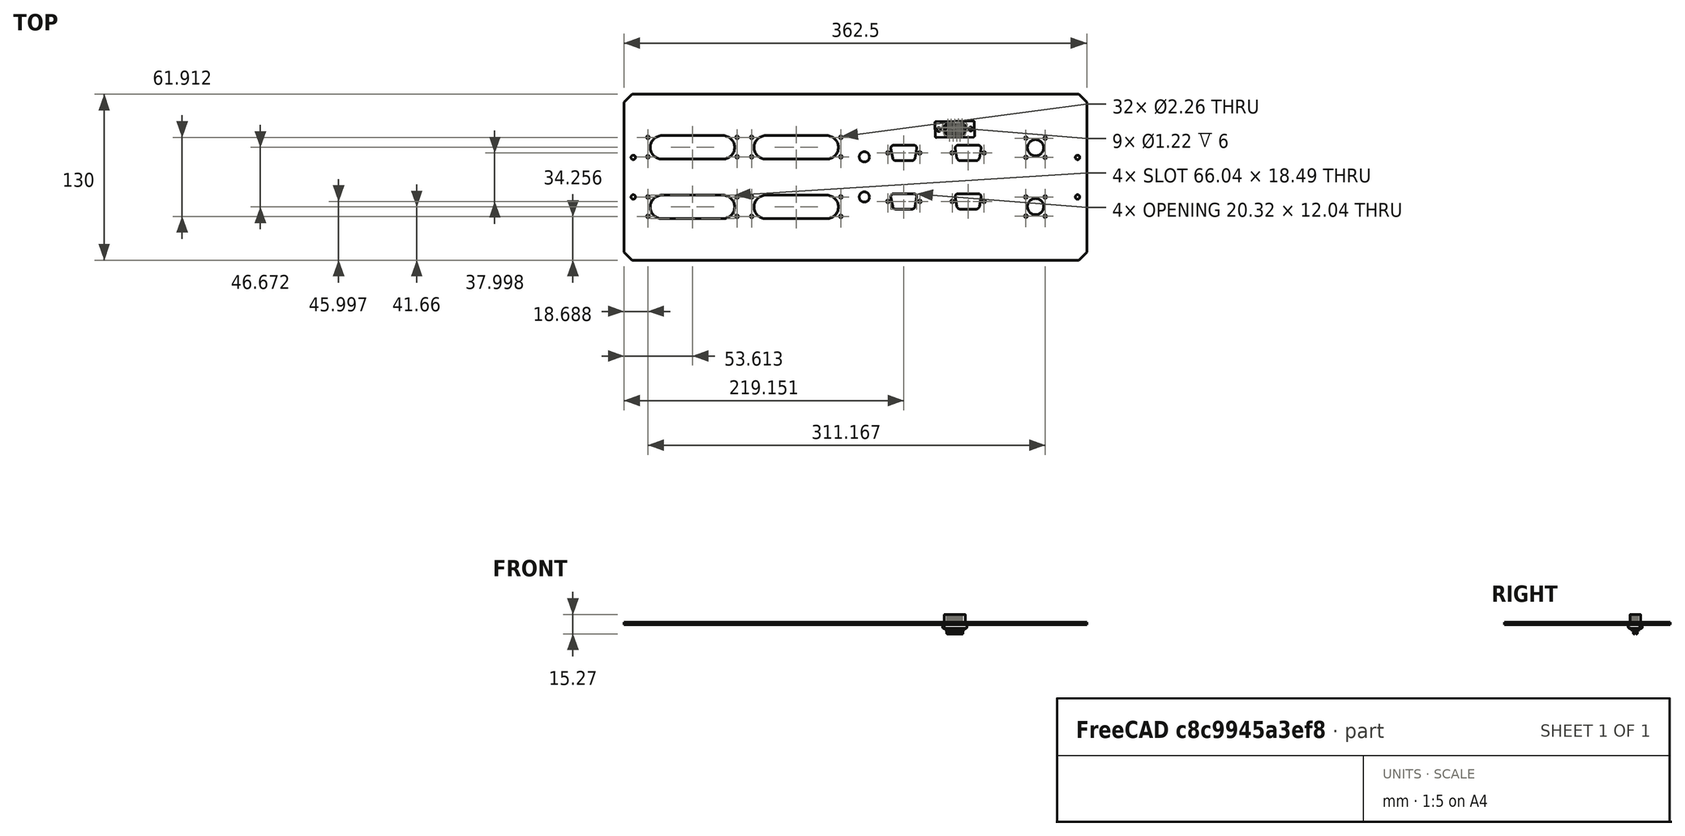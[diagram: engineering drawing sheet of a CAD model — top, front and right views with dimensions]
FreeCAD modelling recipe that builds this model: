
FCSTD DOCUMENT  (FreeCAD 0.20R29603 (Git))
Label: DCT_Front_Panel
License: All rights reserved
LicenseURL: http://en.wikipedia.org/wiki/All_rights_reserved
objects: TechDraw::DrawViewDimension×33, Sketcher::SketchObject×10, TechDraw::DrawViewPart×5, PartDesign::Pocket×4, PartDesign::Line×2, PartDesign::ShapeBinder×2, Part::Refine×1, Part::Feature×1, PartDesign::FeatureBase×1, TechDraw::DrawSVGTemplate×1, TechDraw::DrawViewAnnotation×1, PartDesign::Body×1, TechDraw::DrawPage×1
note: 26 computed .brp shape members not serialized (recipe doc carries the construction recipe); baked Part::Feature solids carry a one-line shape summary decoded from their .brp

FEATURE [Part::Refine] Part__Feature041002002  label="171-009-206"
  Placement = pos=(159.218,43.3941,68.1309) rot=(0,0,1;0.015493rad)
FEATURE [Part::Feature] BaseFeature001  label="Panel001"
  Placement = pos=(44.8215,92.0039,-3.8) rot=(0,0,1;0rad)
  shape: bbox 362.5 x 130 x 2 mm, 14 faces (baked)
FEATURE [PartDesign::FeatureBase] BaseFeature
  BaseFeature = -> BaseFeature001
FEATURE [PartDesign::Line] DatumLine
  AttacherType = Attacher::AttachEngineLine
  Length = 20
  MapMode = 43
  Placement = pos=(51.8643,0,71.9309) rot=(0,0.707107,0.707107;3.14159rad)
  ResizeMode = 0
  Support = -> [BaseFeature]
FEATURE [Sketcher::SketchObject] Sketch002  label="All_Feed_Throughs"
  ExternalGeometry = -> [BaseFeature,DatumLine]
  FullyConstrained = true
  MapMode = 5
  Placement = pos=(0,0,71.9309) rot=(0,0,1;0rad)
  Support = -> [BaseFeature]
  expr: Constraints[103] = Constraints[21]
  expr: Constraints[104] = Constraints[22]
  sketch-geometry (121):
    g0: ArcOfCircle CenterX=-18.2685 CenterY=-53.6783 CenterZ=0 NormalX=0 NormalY=0 NormalZ=1 AngleXU=0 Radius=9.2456 StartAngle=1.5708 EndAngle=4.71239
    g1: ArcOfCircle CenterX=29.2803 CenterY=-53.6783 CenterZ=0 NormalX=0 NormalY=0 NormalZ=1 AngleXU=0 Radius=9.2456 StartAngle=4.71239 EndAngle=7.85398
    g2: LineSegment StartX=-18.2685 StartY=-62.9239 StartZ=0 EndX=29.2803 EndY=-62.9239 EndZ=0
    g3: LineSegment StartX=29.2803 StartY=-44.4327 StartZ=0 EndX=-18.2685 EndY=-44.4327 EndZ=0
    g4: LineSegment StartX=38.5259 StartY=-63.7494 StartZ=0 EndX=38.5259 EndY=-43.6072 EndZ=0
    g5: LineSegment StartX=-27.5141 StartY=-43.6072 StartZ=0 EndX=-27.5141 EndY=-63.7494 EndZ=0
    g6: LineSegment StartX=-32.0861 StartY=-43.6072 StartZ=0 EndX=43.0979 EndY=-43.6072 EndZ=0
    g7: LineSegment StartX=43.0979 StartY=-43.6072 StartZ=0 EndX=43.0979 EndY=-63.7494 EndZ=0
    g8: LineSegment StartX=43.0979 StartY=-63.7494 StartZ=0 EndX=-32.0861 EndY=-63.7494 EndZ=0
    g9: LineSegment StartX=-32.0861 StartY=-63.7494 StartZ=0 EndX=-32.0861 EndY=-43.6072 EndZ=0
    g10: LineSegment StartX=-27.5141 StartY=-53.6783 StartZ=0 EndX=-32.0861 EndY=-53.6783 EndZ=0
    g11: LineSegment StartX=38.5259 StartY=-53.6783 StartZ=0 EndX=43.0979 EndY=-53.6783 EndZ=0
    g12: LineSegment StartX=5.50594 StartY=-44.4327 StartZ=0 EndX=5.50594 EndY=-43.6072 EndZ=0
    g13: LineSegment StartX=5.50594 StartY=-63.7494 StartZ=0 EndX=5.50594 EndY=-62.9239 EndZ=0
    g14: LineSegment StartX=-27.5141 StartY=-53.6783 StartZ=0 EndX=38.5259 EndY=-53.6783 EndZ=0
    g15: LineSegment StartX=5.50594 StartY=-44.4327 StartZ=0 EndX=5.50594 EndY=-62.9239 EndZ=0
    g16: GeomPoint X=5.50594 Y=-53.6783 Z=0
    g17: LineSegment StartX=38.5259 StartY=-43.6072 StartZ=0 EndX=5.50594 EndY=-43.6072 EndZ=0
    g18: LineSegment StartX=5.50594 StartY=-43.6072 StartZ=0 EndX=-27.5141 EndY=-43.6072 EndZ=0
    g19: LineSegment StartX=-27.5141 StartY=-63.7494 StartZ=0 EndX=-32.0861 EndY=-63.7494 EndZ=0
    g20: LineSegment StartX=43.0979 StartY=-63.7494 StartZ=0 EndX=38.5259 EndY=-63.7494 EndZ=0
    g21: Circle CenterX=40.4309 CenterY=-45.8424 CenterZ=0 NormalX=0 NormalY=0 NormalZ=1 AngleXU=0 Radius=1.1303
    g22: Circle CenterX=40.4309 CenterY=-61.0824 CenterZ=0 NormalX=0 NormalY=0 NormalZ=1 AngleXU=0 Radius=1.1303
    g23: Circle CenterX=-29.4191 CenterY=-45.8424 CenterZ=0 NormalX=0 NormalY=0 NormalZ=1 AngleXU=0 Radius=1.1303
    g24: Circle CenterX=-29.4191 CenterY=-61.0824 CenterZ=0 NormalX=0 NormalY=0 NormalZ=1 AngleXU=0 Radius=1.1303
    g25: LineSegment StartX=40.4309 StartY=-61.0824 StartZ=0 EndX=43.0979 EndY=-61.0824 EndZ=0
    g26: LineSegment StartX=40.4309 StartY=-61.0824 StartZ=0 EndX=40.4309 EndY=-63.7494 EndZ=0
    g27: LineSegment StartX=-29.4191 StartY=-61.0824 StartZ=0 EndX=-29.4191 EndY=-63.7494 EndZ=0
    g28: LineSegment StartX=-29.4191 StartY=-61.0824 StartZ=0 EndX=-32.0861 EndY=-61.0824 EndZ=0
    g29: ArcOfCircle CenterX=-99.5518 CenterY=-53.6783 CenterZ=0 NormalX=0 NormalY=0 NormalZ=1 AngleXU=0 Radius=9.2456 StartAngle=1.5708 EndAngle=4.71239
    g30: ArcOfCircle CenterX=-52.003 CenterY=-53.6783 CenterZ=0 NormalX=0 NormalY=0 NormalZ=1 AngleXU=0 Radius=9.2456 StartAngle=4.71239 EndAngle=7.85398
    g31: LineSegment StartX=-99.5518 StartY=-62.9239 StartZ=0 EndX=-52.003 EndY=-62.9239 EndZ=0
    g32: LineSegment StartX=-52.003 StartY=-44.4327 StartZ=0 EndX=-99.5518 EndY=-44.4327 EndZ=0
    g33: LineSegment StartX=-42.7574 StartY=-63.7494 StartZ=0 EndX=-42.7574 EndY=-43.6072 EndZ=0
    g34: LineSegment StartX=-108.797 StartY=-43.6072 StartZ=0 EndX=-108.797 EndY=-63.7494 EndZ=0
    g35: LineSegment StartX=-113.369 StartY=-43.6072 StartZ=0 EndX=-38.1854 EndY=-43.6072 EndZ=0
    g36: LineSegment StartX=-38.1854 StartY=-43.6072 StartZ=0 EndX=-38.1854 EndY=-63.7494 EndZ=0
    g37: LineSegment StartX=-38.1854 StartY=-63.7494 StartZ=0 EndX=-113.369 EndY=-63.7494 EndZ=0
    g38: LineSegment StartX=-113.369 StartY=-63.7494 StartZ=0 EndX=-113.369 EndY=-43.6072 EndZ=0
    g39: LineSegment StartX=-108.797 StartY=-53.6783 StartZ=0 EndX=-113.369 EndY=-53.6783 EndZ=0
    g40: LineSegment StartX=-42.7574 StartY=-53.6783 StartZ=0 EndX=-38.1854 EndY=-53.6783 EndZ=0
    g41: LineSegment StartX=-75.7774 StartY=-44.4327 StartZ=0 EndX=-75.7774 EndY=-43.6072 EndZ=0
    g42: LineSegment StartX=-75.7774 StartY=-63.7494 StartZ=0 EndX=-75.7774 EndY=-62.9239 EndZ=0
    g43: LineSegment StartX=-108.797 StartY=-53.6783 StartZ=0 EndX=-42.7574 EndY=-53.6783 EndZ=0
    g44: LineSegment StartX=-75.7774 StartY=-44.4327 StartZ=0 EndX=-75.7774 EndY=-62.9239 EndZ=0
    g45: GeomPoint X=-75.7774 Y=-53.6783 Z=0
    g46: LineSegment StartX=-42.7574 StartY=-43.6072 StartZ=0 EndX=-75.7774 EndY=-43.6072 EndZ=0
    g47: LineSegment StartX=-75.7774 StartY=-43.6072 StartZ=0 EndX=-108.797 EndY=-43.6072 EndZ=0
    g48: LineSegment StartX=-108.797 StartY=-63.7494 StartZ=0 EndX=-113.369 EndY=-63.7494 EndZ=0
    g49: LineSegment StartX=-38.1854 StartY=-63.7494 StartZ=0 EndX=-42.7574 EndY=-63.7494 EndZ=0
    g50: Circle CenterX=-40.8524 CenterY=-45.8424 CenterZ=0 NormalX=0 NormalY=0 NormalZ=1 AngleXU=0 Radius=1.1303
    g51: Circle CenterX=-40.8524 CenterY=-61.0824 CenterZ=0 NormalX=0 NormalY=0 NormalZ=1 AngleXU=0 Radius=1.1303
    g52: Circle CenterX=-110.702 CenterY=-45.8424 CenterZ=0 NormalX=0 NormalY=0 NormalZ=1 AngleXU=0 Radius=1.1303
    g53: Circle CenterX=-110.702 CenterY=-61.0824 CenterZ=0 NormalX=0 NormalY=0 NormalZ=1 AngleXU=0 Radius=1.1303
    g54: LineSegment StartX=-40.8524 StartY=-61.0824 StartZ=0 EndX=-38.1854 EndY=-61.0824 EndZ=0
    g55: LineSegment StartX=-40.8524 StartY=-61.0824 StartZ=0 EndX=-40.8524 EndY=-63.7494 EndZ=0
    g56: LineSegment StartX=-110.702 StartY=-61.0824 StartZ=0 EndX=-110.702 EndY=-63.7494 EndZ=0
    g57: LineSegment StartX=-110.702 StartY=-61.0824 StartZ=0 EndX=-113.369 EndY=-61.0824 EndZ=0
    g58: ArcOfCircle CenterX=-18.2685 CenterY=-100.35 CenterZ=0 NormalX=0 NormalY=0 NormalZ=1 AngleXU=0 Radius=9.2456 StartAngle=1.5708 EndAngle=4.71239
    g59: ArcOfCircle CenterX=29.2803 CenterY=-100.35 CenterZ=0 NormalX=0 NormalY=0 NormalZ=1 AngleXU=0 Radius=9.2456 StartAngle=4.71239 EndAngle=7.85398
    g60: LineSegment StartX=-18.2685 StartY=-109.596 StartZ=0 EndX=29.2803 EndY=-109.596 EndZ=0
    g61: LineSegment StartX=29.2803 StartY=-91.1045 StartZ=0 EndX=-18.2685 EndY=-91.1045 EndZ=0
    g62: LineSegment StartX=38.5259 StartY=-110.421 StartZ=0 EndX=38.5259 EndY=-90.279 EndZ=0
    g63: LineSegment StartX=-27.5141 StartY=-90.279 StartZ=0 EndX=-27.5141 EndY=-110.421 EndZ=0
    g64: LineSegment StartX=-32.0861 StartY=-90.279 StartZ=0 EndX=43.0979 EndY=-90.279 EndZ=0
    g65: LineSegment StartX=43.0979 StartY=-90.279 StartZ=0 EndX=43.0979 EndY=-110.421 EndZ=0
    g66: LineSegment StartX=43.0979 StartY=-110.421 StartZ=0 EndX=-32.0861 EndY=-110.421 EndZ=0
    g67: LineSegment StartX=-32.0861 StartY=-110.421 StartZ=0 EndX=-32.0861 EndY=-90.279 EndZ=0
    g68: LineSegment StartX=-27.5141 StartY=-100.35 StartZ=0 EndX=-32.0861 EndY=-100.35 EndZ=0
    g69: LineSegment StartX=38.5259 StartY=-100.35 StartZ=0 EndX=43.0979 EndY=-100.35 EndZ=0
    g70: LineSegment StartX=5.50594 StartY=-91.1045 StartZ=0 EndX=5.50594 EndY=-90.279 EndZ=0
    g71: LineSegment StartX=5.50594 StartY=-110.421 StartZ=0 EndX=5.50594 EndY=-109.596 EndZ=0
    g72: LineSegment StartX=-27.5141 StartY=-100.35 StartZ=0 EndX=38.5259 EndY=-100.35 EndZ=0
    g73: LineSegment StartX=5.50594 StartY=-91.1045 StartZ=0 EndX=5.50594 EndY=-109.596 EndZ=0
    g74: GeomPoint X=5.50594 Y=-100.35 Z=0
    g75: LineSegment StartX=38.5259 StartY=-90.279 StartZ=0 EndX=5.50594 EndY=-90.279 EndZ=0
    g76: LineSegment StartX=5.50594 StartY=-90.279 StartZ=0 EndX=-27.5141 EndY=-90.279 EndZ=0
    g77: LineSegment StartX=-27.5141 StartY=-110.421 StartZ=0 EndX=-32.0861 EndY=-110.421 EndZ=0
    g78: LineSegment StartX=43.0979 StartY=-110.421 StartZ=0 EndX=38.5259 EndY=-110.421 EndZ=0
    g79: Circle CenterX=40.4309 CenterY=-92.5142 CenterZ=0 NormalX=0 NormalY=0 NormalZ=1 AngleXU=0 Radius=1.1303
    g80: Circle CenterX=40.4309 CenterY=-107.754 CenterZ=0 NormalX=0 NormalY=0 NormalZ=1 AngleXU=0 Radius=1.1303
    g81: Circle CenterX=-29.4191 CenterY=-92.5142 CenterZ=0 NormalX=0 NormalY=0 NormalZ=1 AngleXU=0 Radius=1.1303
    g82: Circle CenterX=-29.4191 CenterY=-107.754 CenterZ=0 NormalX=0 NormalY=0 NormalZ=1 AngleXU=0 Radius=1.1303
    g83: LineSegment StartX=40.4309 StartY=-107.754 StartZ=0 EndX=43.0979 EndY=-107.754 EndZ=0
    g84: LineSegment StartX=40.4309 StartY=-107.754 StartZ=0 EndX=40.4309 EndY=-110.421 EndZ=0
    g85: LineSegment StartX=-29.4191 StartY=-107.754 StartZ=0 EndX=-29.4191 EndY=-110.421 EndZ=0
    g86: LineSegment StartX=-29.4191 StartY=-107.754 StartZ=0 EndX=-32.0861 EndY=-107.754 EndZ=0
    g87: ArcOfCircle CenterX=-99.5518 CenterY=-100.35 CenterZ=0 NormalX=0 NormalY=0 NormalZ=1 AngleXU=0 Radius=9.2456 StartAngle=1.5708 EndAngle=4.71239
    g88: ArcOfCircle CenterX=-52.003 CenterY=-100.35 CenterZ=0 NormalX=0 NormalY=0 NormalZ=1 AngleXU=0 Radius=9.2456 StartAngle=4.71239 EndAngle=7.85398
    g89: LineSegment StartX=-99.5518 StartY=-109.596 StartZ=0 EndX=-52.003 EndY=-109.596 EndZ=0
    g90: LineSegment StartX=-52.003 StartY=-91.1045 StartZ=0 EndX=-99.5518 EndY=-91.1045 EndZ=0
    g91: LineSegment StartX=-42.7574 StartY=-110.421 StartZ=0 EndX=-42.7574 EndY=-90.279 EndZ=0
    g92: LineSegment StartX=-108.797 StartY=-90.279 StartZ=0 EndX=-108.797 EndY=-110.421 EndZ=0
    g93: LineSegment StartX=-113.369 StartY=-90.279 StartZ=0 EndX=-38.1854 EndY=-90.279 EndZ=0
    g94: LineSegment StartX=-38.1854 StartY=-90.279 StartZ=0 EndX=-38.1854 EndY=-110.421 EndZ=0
    g95: LineSegment StartX=-38.1854 StartY=-110.421 StartZ=0 EndX=-113.369 EndY=-110.421 EndZ=0
    g96: LineSegment StartX=-113.369 StartY=-110.421 StartZ=0 EndX=-113.369 EndY=-90.279 EndZ=0
    g97: LineSegment StartX=-108.797 StartY=-100.35 StartZ=0 EndX=-113.369 EndY=-100.35 EndZ=0
    g98: LineSegment StartX=-42.7574 StartY=-100.35 StartZ=0 EndX=-38.1854 EndY=-100.35 EndZ=0
    g99: LineSegment StartX=-75.7774 StartY=-91.1045 StartZ=0 EndX=-75.7774 EndY=-90.279 EndZ=0
    g100: LineSegment StartX=-75.7774 StartY=-110.421 StartZ=0 EndX=-75.7774 EndY=-109.596 EndZ=0
    g101: LineSegment StartX=-108.797 StartY=-100.35 StartZ=0 EndX=-42.7574 EndY=-100.35 EndZ=0
    g102: LineSegment StartX=-75.7774 StartY=-91.1045 StartZ=0 EndX=-75.7774 EndY=-109.596 EndZ=0
    g103: GeomPoint X=-75.7774 Y=-100.35 Z=0
    g104: LineSegment StartX=-42.7574 StartY=-90.279 StartZ=0 EndX=-75.7774 EndY=-90.279 EndZ=0
    g105: LineSegment StartX=-75.7774 StartY=-90.279 StartZ=0 EndX=-108.797 EndY=-90.279 EndZ=0
    g106: LineSegment StartX=-108.797 StartY=-110.421 StartZ=0 EndX=-113.369 EndY=-110.421 EndZ=0
    g107: LineSegment StartX=-38.1854 StartY=-110.421 StartZ=0 EndX=-42.7574 EndY=-110.421 EndZ=0
    g108: Circle CenterX=-40.8524 CenterY=-92.5142 CenterZ=0 NormalX=0 NormalY=0 NormalZ=1 AngleXU=0 Radius=1.1303
    g109: Circle CenterX=-40.8524 CenterY=-107.754 CenterZ=0 NormalX=0 NormalY=0 NormalZ=1 AngleXU=0 Radius=1.1303
    g110: Circle CenterX=-110.702 CenterY=-92.5142 CenterZ=0 NormalX=0 NormalY=0 NormalZ=1 AngleXU=0 Radius=1.1303
    g111: Circle CenterX=-110.702 CenterY=-107.754 CenterZ=0 NormalX=0 NormalY=0 NormalZ=1 AngleXU=0 Radius=1.1303
    g112: LineSegment StartX=-40.8524 StartY=-107.754 StartZ=0 EndX=-38.1854 EndY=-107.754 EndZ=0
    g113: LineSegment StartX=-40.8524 StartY=-107.754 StartZ=0 EndX=-40.8524 EndY=-110.421 EndZ=0
    g114: LineSegment StartX=-110.702 StartY=-107.754 StartZ=0 EndX=-110.702 EndY=-110.421 EndZ=0
    g115: LineSegment StartX=-110.702 StartY=-107.754 StartZ=0 EndX=-113.369 EndY=-107.754 EndZ=0
    g116: LineSegment StartX=-75.7774 StartY=-110.421 StartZ=0 EndX=-75.7774 EndY=-142.014 EndZ=0
    g117: LineSegment StartX=-75.7774 StartY=-43.6072 StartZ=0 EndX=-75.7774 EndY=-12.0142 EndZ=0
    g118: LineSegment StartX=-122.136 StartY=-92.5142 StartZ=0 EndX=-110.702 EndY=-92.5142 EndZ=0
    g119: LineSegment StartX=-40.8524 StartY=-92.5142 StartZ=0 EndX=-29.4191 EndY=-92.5142 EndZ=0
    g120: LineSegment StartX=40.4309 StartY=-92.5142 StartZ=0 EndX=51.8643 EndY=-92.5142 EndZ=0
  constraints (349):
    c: Tangent(g0,g2) = -1.5708
    c: Tangent(g2,g1) = -1.5708
    c: Tangent(g1,g3) = -1.5708
    c: Tangent(g3,g0) = -1.5708
    c: DistanceY(g1,g1) = 18.4912
    c: Horizontal(g1,g0)
    c: Horizontal(g0,g1)
    c: Vertical(g4)
    c: Vertical(g5)
    c: Tangent(g5,g0)
    c: Tangent(g4,g1)
    c: Horizontal(g5,g4)
    c: DistanceX(g5,g4) = 66.04
    c: Coincident(g6,g7)
    c: Coincident(g7,g8)
    c: Coincident(g8,g9)
    c: Coincident(g9,g6)
    c: Horizontal(g6)
    c: Horizontal(g8)
    c: Vertical(g7)
    c: Vertical(g9)
    c: DistanceX(g6,g6) = 75.184
    c: DistanceY(g7,g7) = 20.1422
    c: PointOnObject(g10,g5)
    c: PointOnObject(g10,g9)
    c: Horizontal(g10)
    c: PointOnObject(g11,g4)
    c: PointOnObject(g11,g7)
    c: Horizontal(g11)
    c: Equal(g11,g10)
    c: PointOnObject(g12,g3)
    c: PointOnObject(g12,g6)
    c: Vertical(g12)
    c: PointOnObject(g13,g8)
    c: PointOnObject(g13,g2)
    c: Vertical(g13)
    c: Equal(g13,g12)
    c: Equal(g5,g9)
    c: Horizontal(g5,g6)
    c: Horizontal(g0,g10)
    c: Horizontal(g1,g11)
    c: Coincident(g14,g10)
    c: Coincident(g14,g11)
    c: Coincident(g15,g12)
    c: Coincident(g15,g13)
    c: Vertical(g15)
    c: PointOnObject(g16,g14)
    c: Vertical(g16,g12)
    c: Horizontal(g4,g6)
    c: Coincident(g17,g4)
    c: Coincident(g17,g12)
    c: Coincident(g18,g12)
    c: Coincident(g18,g5)
    c: Equal(g17,g18)
    c: Coincident(g19,g5)
    c: Coincident(g19,g8)
    c: Coincident(g20,g7)
    c: Coincident(g20,g4)
    c: Vertical(g22,g21)
    c: Diameter(g23) = 2.2606
    c: Vertical(g23,g24)
    c: Horizontal(g24,g22)
    c: Horizontal(g23,g21)
    c: DistanceY(g22,g21) = 15.24
    c: DistanceX(g24,g22) = 69.85
    c: Coincident(g25,g22)
    c: PointOnObject(g25,g7)
    c: Horizontal(g25)
    c: Coincident(g26,g22)
    c: PointOnObject(g26,g8)
    c: Vertical(g26)
    c: Equal(g25,g26)
    c: Coincident(g27,g24)
    c: PointOnObject(g27,g8)
    c: Vertical(g27)
    c: Coincident(g28,g24)
    c: PointOnObject(g28,g9)
    c: Horizontal(g28)
    c: Equal(g28,g27)
    c: Equal(g24,g23)
    c: Equal(g23,g21)
    c: Equal(g21,g22)
    c: Tangent(g29,g31) = -1.5708
    c: Tangent(g31,g30) = -1.5708
    c: Tangent(g30,g32) = -1.5708
    c: Tangent(g32,g29) = -1.5708
    c: DistanceY(g30,g30) = 18.4912
    c: Horizontal(g30,g29)
    c: Horizontal(g29,g30)
    c: Vertical(g33)
    c: Vertical(g34)
    c: Tangent(g34,g29)
    c: Tangent(g33,g30)
    c: Horizontal(g34,g33)
    c: DistanceX(g34,g33) = 66.04
    c: Coincident(g35,g36)
    c: Coincident(g36,g37)
    c: Coincident(g37,g38)
    c: Coincident(g38,g35)
    c: Horizontal(g35)
    c: Horizontal(g37)
    c: Vertical(g36)
    c: Vertical(g38)
    c: DistanceX(g35,g35) = 75.184
    c: DistanceY(g36,g36) = 20.1422
    c: PointOnObject(g39,g34)
    c: PointOnObject(g39,g38)
    c: Horizontal(g39)
    c: PointOnObject(g40,g33)
    c: PointOnObject(g40,g36)
    c: Horizontal(g40)
    c: Equal(g40,g39)
    c: PointOnObject(g41,g32)
    c: PointOnObject(g41,g35)
    c: Vertical(g41)
    c: PointOnObject(g42,g37)
    c: PointOnObject(g42,g31)
    c: Vertical(g42)
    c: Equal(g42,g41)
    c: Equal(g34,g38)
    c: Horizontal(g34,g35)
    c: Horizontal(g29,g39)
    c: Horizontal(g30,g40)
    c: Coincident(g43,g39)
    c: Coincident(g43,g40)
    c: Coincident(g44,g41)
    c: Coincident(g44,g42)
    c: Vertical(g44)
    c: PointOnObject(g45,g43)
    c: Vertical(g45,g41)
    c: Horizontal(g33,g35)
    c: Coincident(g46,g33)
    c: Coincident(g46,g41)
    c: Coincident(g47,g41)
    c: Coincident(g47,g34)
    c: Equal(g46,g47)
    c: Coincident(g48,g34)
    c: Coincident(g48,g37)
    c: Coincident(g49,g36)
    c: Coincident(g49,g33)
    c: Vertical(g51,g50)
    c: Diameter(g52) = 2.2606
    c: Vertical(g52,g53)
    c: Horizontal(g53,g51)
    c: Horizontal(g52,g50)
    c: DistanceY(g51,g50) = 15.24
    c: DistanceX(g53,g51) = 69.85
    c: Coincident(g54,g51)
    c: PointOnObject(g54,g36)
    c: Horizontal(g54)
    c: Coincident(g55,g51)
    c: PointOnObject(g55,g37)
    c: Vertical(g55)
    c: Equal(g54,g55)
    c: Coincident(g56,g53)
    c: PointOnObject(g56,g37)
    c: Vertical(g56)
    c: Coincident(g57,g53)
    c: PointOnObject(g57,g38)
    c: Horizontal(g57)
    c: Equal(g57,g56)
    c: Equal(g53,g52)
    c: Equal(g52,g50)
    c: Equal(g50,g51)
    c: Tangent(g58,g60) = -1.5708
    c: Tangent(g60,g59) = -1.5708
    c: Tangent(g59,g61) = -1.5708
    c: Tangent(g61,g58) = -1.5708
    c: DistanceY(g59,g59) = 18.4912
    c: Horizontal(g59,g58)
    c: Horizontal(g58,g59)
    c: Vertical(g62)
    c: Vertical(g63)
    c: Tangent(g63,g58)
    c: Tangent(g62,g59)
    c: Horizontal(g63,g62)
    c: DistanceX(g63,g62) = 66.04
    c: Coincident(g64,g65)
    c: Coincident(g65,g66)
    c: Coincident(g66,g67)
    c: Coincident(g67,g64)
    c: Horizontal(g64)
    c: Horizontal(g66)
    c: Vertical(g65)
    c: Vertical(g67)
    c: DistanceX(g64,g64) = 75.184
    c: DistanceY(g65,g65) = 20.1422
    c: PointOnObject(g68,g63)
    c: PointOnObject(g68,g67)
    c: Horizontal(g68)
    c: PointOnObject(g69,g62)
    c: PointOnObject(g69,g65)
    c: Horizontal(g69)
    c: Equal(g69,g68)
    c: PointOnObject(g70,g61)
    c: PointOnObject(g70,g64)
    c: Vertical(g70)
    c: PointOnObject(g71,g66)
    c: PointOnObject(g71,g60)
    c: Vertical(g71)
    c: Equal(g71,g70)
    c: Equal(g63,g67)
    c: Horizontal(g63,g64)
    c: Horizontal(g58,g68)
    c: Horizontal(g59,g69)
    c: Coincident(g72,g68)
    c: Coincident(g72,g69)
    c: Coincident(g73,g70)
    c: Coincident(g73,g71)
    c: Vertical(g73)
    c: PointOnObject(g74,g72)
    c: Vertical(g74,g70)
    c: Horizontal(g62,g64)
    c: Coincident(g75,g62)
    c: Coincident(g75,g70)
    c: Coincident(g76,g70)
    c: Coincident(g76,g63)
    c: Equal(g75,g76)
    c: Coincident(g77,g63)
    c: Coincident(g77,g66)
    c: Coincident(g78,g65)
    c: Coincident(g78,g62)
    c: Vertical(g80,g79)
    c: Diameter(g81) = 2.2606
    c: Vertical(g81,g82)
    c: Horizontal(g82,g80)
    c: Horizontal(g81,g79)
    c: DistanceY(g80,g79) = 15.24
    c: DistanceX(g82,g80) = 69.85
    c: Coincident(g83,g80)
    c: PointOnObject(g83,g65)
    c: Horizontal(g83)
    c: Coincident(g84,g80)
    c: PointOnObject(g84,g66)
    c: Vertical(g84)
    c: Equal(g83,g84)
    c: Coincident(g85,g82)
    c: PointOnObject(g85,g66)
    c: Vertical(g85)
    c: Coincident(g86,g82)
    c: PointOnObject(g86,g67)
    c: Horizontal(g86)
    c: Equal(g86,g85)
    c: Equal(g82,g81)
    c: Equal(g81,g79)
    c: Equal(g79,g80)
    c: Tangent(g87,g89) = -1.5708
    c: Tangent(g89,g88) = -1.5708
    c: Tangent(g88,g90) = -1.5708
    c: Tangent(g90,g87) = -1.5708
    c: DistanceY(g88,g88) = 18.4912
    c: Horizontal(g88,g87)
    c: Horizontal(g87,g88)
    c: Vertical(g91)
    c: Vertical(g92)
    c: Tangent(g92,g87)
    c: Tangent(g91,g88)
    c: Horizontal(g92,g91)
    c: DistanceX(g92,g91) = 66.04
    c: Coincident(g93,g94)
    c: Coincident(g94,g95)
    c: Coincident(g95,g96)
    c: Coincident(g96,g93)
    c: Horizontal(g93)
    c: Horizontal(g95)
    c: Vertical(g94)
    c: Vertical(g96)
    c: DistanceX(g93,g93) = 75.184
    c: DistanceY(g94,g94) = 20.1422
    c: PointOnObject(g97,g92)
    c: PointOnObject(g97,g96)
    c: Horizontal(g97)
    c: PointOnObject(g98,g91)
    c: PointOnObject(g98,g94)
    c: Horizontal(g98)
    c: Equal(g98,g97)
    c: PointOnObject(g99,g90)
    c: PointOnObject(g99,g93)
    c: Vertical(g99)
    c: PointOnObject(g100,g95)
    c: PointOnObject(g100,g89)
    c: Vertical(g100)
    c: Equal(g100,g99)
    c: Equal(g92,g96)
    c: Horizontal(g92,g93)
    c: Horizontal(g87,g97)
    c: Horizontal(g88,g98)
    c: Coincident(g101,g97)
    c: Coincident(g101,g98)
    c: Coincident(g102,g99)
    c: Coincident(g102,g100)
    c: Vertical(g102)
    c: PointOnObject(g103,g101)
    c: Vertical(g103,g99)
    c: Horizontal(g91,g93)
    c: Coincident(g104,g91)
    c: Coincident(g104,g99)
    c: Coincident(g105,g99)
    c: Coincident(g105,g92)
    c: Equal(g104,g105)
    c: Coincident(g106,g92)
    c: Coincident(g106,g95)
    c: Coincident(g107,g94)
    c: Coincident(g107,g91)
    c: Vertical(g109,g108)
    c: Diameter(g110) = 2.2606
    c: Vertical(g110,g111)
    c: Horizontal(g111,g109)
    c: Horizontal(g110,g108)
    c: DistanceY(g109,g108) = 15.24
    c: DistanceX(g111,g109) = 69.85
    c: Coincident(g112,g109)
    c: PointOnObject(g112,g94)
    c: Horizontal(g112)
    c: Coincident(g113,g109)
    c: PointOnObject(g113,g95)
    c: Vertical(g113)
    c: Equal(g112,g113)
    c: Coincident(g114,g111)
    c: PointOnObject(g114,g95)
    c: Vertical(g114)
    c: Coincident(g115,g111)
    c: PointOnObject(g115,g96)
    c: Horizontal(g115)
    c: Equal(g115,g114)
    c: Equal(g111,g110)
    c: Equal(g110,g108)
    c: Equal(g108,g109)
    c: Vertical(g23,g81)
    c: Vertical(g52,g110)
    c: Horizontal(g110,g79)
    c: Horizontal(g52,g21)
    c: Coincident(g116,g100)
    c: PointOnObject(g116,g-4)
    c: Vertical(g116)
    c: Coincident(g117,g41)
    c: PointOnObject(g117,g-3)
    c: Vertical(g117)
    c: Equal(g117,g116)
    c: Coincident(g118,g-6)
    c: Coincident(g118,g110)
    c: Horizontal(g118)
    c: Coincident(g119,g108)
    c: Coincident(g119,g81)
    c: Coincident(g120,g79)
    c: PointOnObject(g120,g-8)
    c: Horizontal(g120)
    c: Equal(g120,g118)
    c: Equal(g119,g120)
FEATURE [PartDesign::Line] DatumLine001
  AttacherType = Attacher::AttachEngineLine
  Length = 20
  MapMode = 44
  Placement = pos=(7.1e-15,-77.0142,71.9309) rot=(0.57735,0.57735,0.57735;2.0944rad)
  ResizeMode = 0
  Support = -> [BaseFeature]
FEATURE [PartDesign::ShapeBinder] ReferencePart__Feature041002002  label="Ref_front_dsub"
  Placement = pos=(159.218,43.3941,68.1309) rot=(0,0,1;0.015493rad)
  Support = -> [Part__Feature041002002]
  TraceSupport = false
FEATURE [PartDesign::ShapeBinder] ReferencePart__Feature041002002001  label="Ref_back_Dsub"
  Placement = pos=(159.218,43.3941,68.1309) rot=(0,0,1;0.015493rad)
  Support = -> [Part__Feature041002002]
  TraceSupport = false
FEATURE [Sketcher::SketchObject] Sketch008  label="DSub_single"
  FullyConstrained = false
  MapMode = 5
  Placement = pos=(159.218,43.3941,67.2309) rot=(0.99997,0.007746,0;3.14159rad)
  Support = -> [ReferencePart__Feature041002002001]
  sketch-geometry (44):
    g0: LineSegment StartX=0.8871 StartY=0.0324575 StartZ=0 EndX=29.8834 EndY=0.0324575 EndZ=0
    g1: LineSegment StartX=30.7903 StartY=-0.87451 StartZ=0 EndX=30.7903 EndY=-11.659 EndZ=0
    g2: LineSegment StartX=29.8834 StartY=-12.5659 StartZ=0 EndX=0.8871 EndY=-12.5659 EndZ=0
    g3: LineSegment StartX=-0.0198673 StartY=-11.659 StartZ=0 EndX=-0.0198673 EndY=-0.87451 EndZ=0
    g4: LineSegment StartX=9.03056 StartY=-0.245927 StartZ=0 EndX=21.7399 EndY=-0.245927 EndZ=0
    g5: LineSegment StartX=22.7172 StartY=-12.2876 StartZ=0 EndX=8.05325 EndY=-12.2876 EndZ=0
    g6: LineSegment StartX=6.62223 StartY=-2.11273 StartZ=0 EndX=5.22523 EndY=-9.60357 EndZ=0
    g7: LineSegment StartX=24.1482 StartY=-2.11273 StartZ=0 EndX=25.5452 EndY=-9.60357 EndZ=0
    g8: Circle CenterX=2.88843 CenterY=-6.26674 CenterZ=0 NormalX=0 NormalY=0 NormalZ=1 AngleXU=0 Radius=1.1303
    g9: Circle CenterX=27.882 CenterY=-6.26674 CenterZ=0 NormalX=0 NormalY=0 NormalZ=1 AngleXU=0 Radius=1.1303
    g10: ArcOfCircle CenterX=0.8871 CenterY=-0.87451 CenterZ=0 NormalX=0 NormalY=0 NormalZ=1 AngleXU=0 Radius=0.906967 StartAngle=1.5708 EndAngle=3.14159
    g11: ArcOfCircle CenterX=29.8834 CenterY=-0.87451 CenterZ=0 NormalX=0 NormalY=0 NormalZ=1 AngleXU=0 Radius=0.906967 StartAngle=0 EndAngle=1.5708
    g12: ArcOfCircle CenterX=29.8834 CenterY=-11.659 CenterZ=0 NormalX=0 NormalY=0 NormalZ=1 AngleXU=0 Radius=0.906967 StartAngle=4.71239 EndAngle=6.28319
    g13: ArcOfCircle CenterX=23.0052 CenterY=-9.75907 CenterZ=0 NormalX=0 NormalY=0 NormalZ=1 AngleXU=0 Radius=2.54483 StartAngle=4.599 EndAngle=6.34433
    g14: ArcOfCircle CenterX=7.76531 CenterY=-9.75907 CenterZ=0 NormalX=0 NormalY=0 NormalZ=1 AngleXU=0 Radius=2.54483 StartAngle=3.08045 EndAngle=4.82578
    g15: ArcOfCircle CenterX=9.04283 CenterY=-2.74862 CenterZ=0 NormalX=0 NormalY=0 NormalZ=1 AngleXU=0 Radius=2.50273 StartAngle=1.5757 EndAngle=2.88469
    g16: ArcOfCircle CenterX=21.7276 CenterY=-2.74862 CenterZ=0 NormalX=0 NormalY=0 NormalZ=1 AngleXU=0 Radius=2.50273 StartAngle=0.256898 EndAngle=1.5659
    g17: ArcOfCircle CenterX=0.8871 CenterY=-11.659 CenterZ=0 NormalX=0 NormalY=0 NormalZ=1 AngleXU=0 Radius=0.906967 StartAngle=3.14159 EndAngle=4.71239
    g18: LineSegment StartX=29.8834 StartY=0.0324575 StartZ=0 EndX=29.8834 EndY=-0.87451 EndZ=0
    g19: LineSegment StartX=29.8834 StartY=-0.87451 StartZ=0 EndX=30.7903 EndY=-0.87451 EndZ=0
    g20: LineSegment StartX=2.88843 StartY=-6.26674 StartZ=0 EndX=-0.0198673 EndY=-6.26674 EndZ=0
    g21: LineSegment StartX=27.882 StartY=-6.26674 StartZ=0 EndX=30.7903 EndY=-6.26674 EndZ=0
    g22: LineSegment StartX=2.88843 StartY=-6.26674 StartZ=0 EndX=2.88843 EndY=-12.5659 EndZ=0
    g23: LineSegment StartX=27.882 StartY=-6.26674 StartZ=0 EndX=27.882 EndY=-12.5659 EndZ=0
    g24: LineSegment StartX=2.88843 StartY=-6.26674 StartZ=0 EndX=2.88843 EndY=0.0324575 EndZ=0
    g25: LineSegment StartX=27.882 StartY=-6.26674 StartZ=0 EndX=27.882 EndY=0.0324575 EndZ=0
    g26: LineSegment StartX=2.88843 StartY=-6.26674 StartZ=0 EndX=27.882 EndY=-6.26674 EndZ=0
    g27: LineSegment StartX=14.6434 StartY=0.0324575 StartZ=0 EndX=14.6434 EndY=-0.245927 EndZ=0
    g28: LineSegment StartX=14.6434 StartY=-12.2876 StartZ=0 EndX=14.6434 EndY=-12.5659 EndZ=0
    g29: LineSegment StartX=24.9229 StartY=-6.26674 StartZ=0 EndX=26.7517 EndY=-6.26674 EndZ=0
    g30: LineSegment StartX=5.84753 StartY=-6.26674 StartZ=0 EndX=2.88843 EndY=-6.26674 EndZ=0
    g31: LineSegment StartX=6.62223 StartY=-2.11273 StartZ=0 EndX=-0.0198673 EndY=-2.11273 EndZ=0
    g32: LineSegment StartX=5.22523 StartY=-9.60357 StartZ=0 EndX=-0.0198673 EndY=-9.60357 EndZ=0
    g33: LineSegment StartX=24.1482 StartY=-2.11273 StartZ=0 EndX=30.7903 EndY=-2.11273 EndZ=0
    g34: LineSegment StartX=25.5452 StartY=-9.60357 StartZ=0 EndX=30.7903 EndY=-9.60357 EndZ=0
    g35: GeomPoint X=4.01873 Y=-6.26674 Z=0
    g36: LineSegment StartX=-0.0198673 StartY=-0.87451 StartZ=0 EndX=0.8871 EndY=-0.87451 EndZ=0
    g37: LineSegment StartX=0.8871 StartY=-0.87451 StartZ=0 EndX=0.8871 EndY=0.0324575 EndZ=0
    g38: LineSegment StartX=0.8871 StartY=-12.5659 StartZ=0 EndX=0.8871 EndY=-11.659 EndZ=0
    g39: LineSegment StartX=0.8871 StartY=-11.659 StartZ=0 EndX=-0.0198673 EndY=-11.659 EndZ=0
    g40: LineSegment StartX=29.8834 StartY=-12.5659 StartZ=0 EndX=29.8834 EndY=-11.659 EndZ=0
    g41: LineSegment StartX=29.8834 StartY=-11.659 StartZ=0 EndX=30.7903 EndY=-11.659 EndZ=0
    g42: LineSegment StartX=9.03056 StartY=-0.245927 StartZ=0 EndX=8.05325 EndY=-12.2876 EndZ=0
    g43: LineSegment StartX=21.7399 StartY=-0.245927 StartZ=0 EndX=22.7172 EndY=-12.2876 EndZ=0
  constraints (129):
    c: Equal(g7,g6)
    c: Coincident(g10,g3)
    c: Coincident(g10,g0)
    c: Coincident(g11,g0)
    c: Coincident(g11,g1)
    c: Coincident(g12,g1)
    c: Coincident(g12,g2)
    c: Coincident(g13,g7)
    c: Coincident(g13,g5)
    c: Coincident(g14,g6)
    c: Coincident(g14,g5)
    c: Coincident(g15,g6)
    c: Coincident(g15,g4)
    c: Coincident(g16,g4)
    c: Coincident(g16,g7)
    c: Coincident(g17,g2)
    c: Coincident(g17,g3)
    c: Equal(g8,g9)
    c: Diameter(g8) = 2.2606
    c: DistanceX(g8,g9) = 24.9936
    c: DistanceX(g3,g1) = 30.8102
    c: Parallel(g5,g2)
    c: Parallel(g2,g4)
    c: Parallel(g4,g0)
    c: Parallel(g1,g3)
    c: Perpendicular(g1,g0)
    c: Coincident(g18,g0)
    c: Coincident(g18,g11)
    c: Vertical(g18)
    c: Coincident(g19,g11)
    c: Coincident(g19,g1)
    c: Horizontal(g19)
    c: Vertical(g11,g12)
    c: Vertical(g12,g2)
    c: Horizontal(g1,g12)
    c: Horizontal(g12,g17)
    c: Horizontal(g17,g3)
    c: Vertical(g2,g17)
    c: Vertical(g17,g10)
    c: Vertical(g10,g0)
    c: Horizontal(g3,g10)
    c: Horizontal(g10,g11)
    c: DistanceY(g2,g0) = 12.5984
    c: Coincident(g20,g8)
    c: PointOnObject(g20,g3)
    c: Horizontal(g20)
    c: Coincident(g21,g9)
    c: PointOnObject(g21,g1)
    c: Horizontal(g21)
    c: Equal(g21,g20)
    c: Coincident(g22,g8)
    c: PointOnObject(g22,g2)
    c: Vertical(g22)
    c: Coincident(g23,g9)
    c: PointOnObject(g23,g2)
    c: Vertical(g23)
    c: Coincident(g24,g8)
    c: PointOnObject(g24,g0)
    c: Vertical(g24)
    c: Coincident(g25,g9)
    c: PointOnObject(g25,g0)
    c: Vertical(g25)
    c: Equal(g25,g24)
    c: Equal(g25,g23)
    c: Horizontal(g6,g7)
    c: Horizontal(g7,g6)
    c: PointOnObject(g27,g0)
    c: PointOnObject(g27,g4)
    c: Vertical(g27)
    c: PointOnObject(g28,g5)
    c: PointOnObject(g28,g2)
    c: Equal(g28,g27)
    c: Vertical(g28,g28)
    c: Vertical(g27,g28)
    c: PointOnObject(g29,g7)
    c: PointOnObject(g29,g26)
    c: Horizontal(g29)
    c: PointOnObject(g30,g6)
    c: Coincident(g30,g8)
    c: Horizontal(g30)
    c: Coincident(g26,g8)
    c: Equal(g16,g15)
    c: Equal(g14,g13)
    c: Angle(g16) = 1.309
    c: Angle(g13) = 1.74533
    c: Coincident(g31,g6)
    c: PointOnObject(g31,g3)
    c: Horizontal(g31)
    c: Coincident(g32,g6)
    c: PointOnObject(g32,g3)
    c: Horizontal(g32)
    c: Coincident(g33,g7)
    c: PointOnObject(g33,g1)
    c: Horizontal(g33)
    c: Coincident(g34,g7)
    c: PointOnObject(g34,g1)
    c: Horizontal(g34)
    c: Equal(g34,g32)
    c: PointOnObject(g35,g8)
    c: DistanceX(g35,g30) = 1.8288
    c: DistanceX(g29,g29) = 1.8288
    c: Horizontal(g8,g35)
    c: Angle(g15) = 1.309
    c: Angle(g14) = 1.74533
    c: DistanceX(g6,g7) = 17.526
    c: DistanceX(g6,g7) = 20.32
    c: DistanceX(g20,g30) = 5.8674
    c: DistanceX(g29,g21) = 5.8674
    c: Coincident(g26,g9)
    c: Distance(g7) = 7.62
    c: Coincident(g36,g3)
    c: Coincident(g36,g10)
    c: Coincident(g37,g10)
    c: Coincident(g37,g0)
    c: Coincident(g38,g2)
    c: Coincident(g38,g17)
    c: Coincident(g39,g17)
    c: Coincident(g39,g3)
    c: Coincident(g40,g2)
    c: Coincident(g40,g12)
    c: Coincident(g41,g12)
    c: Coincident(g41,g1)
    c: Coincident(g42,g4)
    c: Coincident(g42,g5)
    c: Coincident(g43,g4)
    c: Coincident(g43,g5)
    c: Angle(g42,g26) = 1.65178
    c: DistanceY(g27,g27) = 0.278384
    c: DistanceX(g27,g0) = 15.24
FEATURE [Sketcher::SketchObject] Sketch009  label="DSub_single001"
  AttachmentOffset = pos=(0,0,0) rot=(0,0,1;1.5708rad)
  FullyConstrained = false
  MapMode = 45
  Placement = pos=(51.8643,-77.0142,71.9309) rot=(0,0,1;3.14159rad)
  Support = -> [BaseFeature]
  expr: .Placement.Base.z = 2.83
  sketch-geometry (43):
    g0: LineSegment StartX=-28.0541 StartY=-1.04386 StartZ=0 EndX=1.09896 EndY=-1.04386 EndZ=0
    g1: LineSegment StartX=1.92751 StartY=-1.8724 StartZ=0 EndX=1.92751 EndY=-12.8137 EndZ=0
    g2: LineSegment StartX=1.09896 StartY=-13.6423 StartZ=0 EndX=-28.0541 EndY=-13.6423 EndZ=0
    g3: LineSegment StartX=-28.8827 StartY=-12.8137 StartZ=0 EndX=-28.8827 EndY=-1.8724 EndZ=0
    g4: LineSegment StartX=-20.0816 StartY=-1.32224 StartZ=0 EndX=-6.87359 EndY=-1.32224 EndZ=0
    g5: LineSegment StartX=-5.85759 StartY=-13.3639 StartZ=0 EndX=-21.0976 EndY=-13.3639 EndZ=0
    g6: LineSegment StartX=-22.2406 StartY=-3.35741 StartZ=0 EndX=-23.6376 EndY=-10.8483 EndZ=0
    g7: LineSegment StartX=-4.71459 StartY=-3.35741 StartZ=0 EndX=-3.31759 EndY=-10.8483 EndZ=0
    g8: Circle CenterX=-25.9744 CenterY=-7.34306 CenterZ=0 NormalX=0 NormalY=0 NormalZ=1 AngleXU=0 Radius=1.1303
    g9: Circle CenterX=-0.980793 CenterY=-7.34306 CenterZ=0 NormalX=0 NormalY=0 NormalZ=1 AngleXU=0 Radius=1.1303
    g10: ArcOfCircle CenterX=-28.0541 CenterY=-1.8724 CenterZ=0 NormalX=0 NormalY=0 NormalZ=1 AngleXU=0 Radius=0.828548 StartAngle=1.5708 EndAngle=3.14159
    g11: ArcOfCircle CenterX=1.09896 CenterY=-1.8724 CenterZ=0 NormalX=0 NormalY=0 NormalZ=1 AngleXU=0 Radius=0.828548 StartAngle=0 EndAngle=1.5708
    g12: ArcOfCircle CenterX=1.09896 CenterY=-12.8137 CenterZ=0 NormalX=0 NormalY=0 NormalZ=1 AngleXU=0 Radius=0.828548 StartAngle=4.71239 EndAngle=6.28319
    g13: ArcOfCircle CenterX=-5.64302 CenterY=-11.0404 CenterZ=0 NormalX=0 NormalY=0 NormalZ=1 AngleXU=0 Radius=2.33335 StartAngle=4.6203 EndAngle=6.36563
    g14: ArcOfCircle CenterX=-21.3122 CenterY=-11.0404 CenterZ=0 NormalX=0 NormalY=0 NormalZ=1 AngleXU=0 Radius=2.33335 StartAngle=3.05915 EndAngle=4.80448
    g15: ArcOfCircle CenterX=-19.835 CenterY=-3.74666 CenterZ=0 NormalX=0 NormalY=0 NormalZ=1 AngleXU=0 Radius=2.43693 StartAngle=1.67218 EndAngle=2.98118
    g16: ArcOfCircle CenterX=-7.12023 CenterY=-3.74666 CenterZ=0 NormalX=0 NormalY=0 NormalZ=1 AngleXU=0 Radius=2.43693 StartAngle=0.160416 EndAngle=1.46941
    g17: ArcOfCircle CenterX=-28.0541 CenterY=-12.8137 CenterZ=0 NormalX=0 NormalY=0 NormalZ=1 AngleXU=0 Radius=0.828548 StartAngle=3.14159 EndAngle=4.71239
    g18: LineSegment StartX=1.09896 StartY=-1.04386 StartZ=0 EndX=1.09896 EndY=-1.8724 EndZ=0
    g19: LineSegment StartX=1.09896 StartY=-1.8724 StartZ=0 EndX=1.92751 EndY=-1.8724 EndZ=0
    g20: LineSegment StartX=-25.9744 StartY=-7.34306 StartZ=0 EndX=-28.8827 EndY=-7.34306 EndZ=0
    g21: LineSegment StartX=-0.980793 StartY=-7.34306 StartZ=0 EndX=1.92751 EndY=-7.34306 EndZ=0
    g22: LineSegment StartX=-25.9744 StartY=-7.34306 StartZ=0 EndX=-25.9744 EndY=-13.6423 EndZ=0
    g23: LineSegment StartX=-0.980793 StartY=-7.34306 StartZ=0 EndX=-0.980793 EndY=-13.6423 EndZ=0
    g24: LineSegment StartX=-25.9744 StartY=-7.34306 StartZ=0 EndX=-25.9744 EndY=-1.04386 EndZ=0
    g25: LineSegment StartX=-0.980793 StartY=-7.34306 StartZ=0 EndX=-0.980793 EndY=-1.04386 EndZ=0
    g26: LineSegment StartX=-14.141 StartY=-1.04386 StartZ=0 EndX=-14.141 EndY=-1.32224 EndZ=0
    g27: LineSegment StartX=-14.141 StartY=-13.3639 StartZ=0 EndX=-14.141 EndY=-13.6423 EndZ=0
    g28: LineSegment StartX=-3.97129 StartY=-7.34306 StartZ=0 EndX=-0.980793 EndY=-7.34306 EndZ=0
    g29: LineSegment StartX=-22.9839 StartY=-7.34306 StartZ=0 EndX=-25.9744 EndY=-7.34306 EndZ=0
    g30: LineSegment StartX=-22.2406 StartY=-3.35741 StartZ=0 EndX=-28.8827 EndY=-3.35741 EndZ=0
    g31: LineSegment StartX=-23.6376 StartY=-10.8483 StartZ=0 EndX=-28.8827 EndY=-10.8483 EndZ=0
    g32: LineSegment StartX=-4.71459 StartY=-3.35741 StartZ=0 EndX=1.92751 EndY=-3.35741 EndZ=0
    g33: LineSegment StartX=-3.31759 StartY=-10.8483 StartZ=0 EndX=1.92751 EndY=-10.8483 EndZ=0
    g34: GeomPoint X=-24.8441 Y=-7.34306 Z=0
    g35: LineSegment StartX=-28.8827 StartY=-1.8724 StartZ=0 EndX=-28.0541 EndY=-1.8724 EndZ=0
    g36: LineSegment StartX=-28.0541 StartY=-1.8724 StartZ=0 EndX=-28.0541 EndY=-1.04386 EndZ=0
    g37: LineSegment StartX=-28.0541 StartY=-13.6423 StartZ=0 EndX=-28.0541 EndY=-12.8137 EndZ=0
    g38: LineSegment StartX=-28.0541 StartY=-12.8137 StartZ=0 EndX=-28.8827 EndY=-12.8137 EndZ=0
    g39: LineSegment StartX=1.09896 StartY=-13.6423 StartZ=0 EndX=1.09896 EndY=-12.8137 EndZ=0
    g40: LineSegment StartX=1.09896 StartY=-12.8137 StartZ=0 EndX=1.92751 EndY=-12.8137 EndZ=0
    g41: LineSegment StartX=-20.0816 StartY=-1.32224 StartZ=0 EndX=-21.0976 EndY=-13.3639 EndZ=0
    g42: LineSegment StartX=-6.87359 StartY=-1.32224 StartZ=0 EndX=-5.85759 EndY=-13.3639 EndZ=0
  constraints (128):
    c: Equal(g7,g6)
    c: Coincident(g10,g3)
    c: Coincident(g10,g0)
    c: Coincident(g11,g0)
    c: Coincident(g11,g1)
    c: Coincident(g12,g1)
    c: Coincident(g12,g2)
    c: Coincident(g13,g7)
    c: Coincident(g13,g5)
    c: Coincident(g14,g6)
    c: Coincident(g14,g5)
    c: Coincident(g15,g6)
    c: Coincident(g15,g4)
    c: Coincident(g16,g4)
    c: Coincident(g16,g7)
    c: Coincident(g17,g2)
    c: Coincident(g17,g3)
    c: Equal(g8,g9)
    c: Diameter(g8) = 2.2606
    c: DistanceX(g8,g9) = 24.9936
    c: DistanceX(g3,g1) = 30.8102
    c: Parallel(g5,g2)
    c: Parallel(g2,g4)
    c: Parallel(g4,g0)
    c: Parallel(g1,g3)
    c: Perpendicular(g1,g0)
    c: Coincident(g18,g0)
    c: Coincident(g18,g11)
    c: Vertical(g18)
    c: Coincident(g19,g11)
    c: Coincident(g19,g1)
    c: Horizontal(g19)
    c: Vertical(g11,g12)
    c: Vertical(g12,g2)
    c: Horizontal(g1,g12)
    c: Horizontal(g12,g17)
    c: Horizontal(g17,g3)
    c: Vertical(g2,g17)
    c: Vertical(g17,g10)
    c: Vertical(g10,g0)
    c: Horizontal(g3,g10)
    c: Horizontal(g10,g11)
    c: DistanceY(g2,g0) = 12.5984
    c: Coincident(g20,g8)
    c: PointOnObject(g20,g3)
    c: Horizontal(g20)
    c: Coincident(g21,g9)
    c: PointOnObject(g21,g1)
    c: Horizontal(g21)
    c: Equal(g21,g20)
    c: Coincident(g22,g8)
    c: PointOnObject(g22,g2)
    c: Vertical(g22)
    c: Coincident(g23,g9)
    c: PointOnObject(g23,g2)
    c: Vertical(g23)
    c: Coincident(g24,g8)
    c: PointOnObject(g24,g0)
    c: Vertical(g24)
    c: Coincident(g25,g9)
    c: PointOnObject(g25,g0)
    c: Vertical(g25)
    c: Equal(g25,g24)
    c: Equal(g25,g23)
    c: Horizontal(g6,g7)
    c: Horizontal(g7,g6)
    c: PointOnObject(g26,g0)
    c: PointOnObject(g26,g4)
    c: Vertical(g26)
    c: PointOnObject(g27,g5)
    c: PointOnObject(g27,g2)
    c: Equal(g27,g26)
    c: Vertical(g27,g27)
    c: Vertical(g26,g27)
    c: PointOnObject(g28,g7)
    c: Horizontal(g28)
    c: PointOnObject(g29,g6)
    c: Coincident(g29,g8)
    c: Horizontal(g29)
    c: Equal(g16,g15)
    c: Equal(g14,g13)
    c: Angle(g16) = 1.309
    c: Angle(g13) = 1.74533
    c: Coincident(g30,g6)
    c: PointOnObject(g30,g3)
    c: Horizontal(g30)
    c: Coincident(g31,g6)
    c: PointOnObject(g31,g3)
    c: Horizontal(g31)
    c: Coincident(g32,g7)
    c: PointOnObject(g32,g1)
    c: Horizontal(g32)
    c: Coincident(g33,g7)
    c: PointOnObject(g33,g1)
    c: Horizontal(g33)
    c: Equal(g33,g31)
    c: PointOnObject(g34,g8)
    c: Horizontal(g8,g34)
    c: Angle(g15) = 1.309
    c: Angle(g14) = 1.74533
    c: DistanceX(g6,g7) = 17.526
    c: DistanceX(g6,g7) = 20.32
    c: DistanceX(g20,g29) = 5.8988
    c: DistanceX(g28,g21) = 5.8988
    c: Distance(g7) = 7.62
    c: Coincident(g35,g3)
    c: Coincident(g35,g10)
    c: Coincident(g36,g10)
    c: Coincident(g36,g0)
    c: Coincident(g37,g2)
    c: Coincident(g37,g17)
    c: Coincident(g38,g17)
    c: Coincident(g38,g3)
    c: Coincident(g39,g2)
    c: Coincident(g39,g12)
    c: Coincident(g40,g12)
    c: Coincident(g40,g1)
    c: Coincident(g41,g4)
    c: Coincident(g41,g5)
    c: Coincident(g42,g4)
    c: Coincident(g42,g5)
    c: DistanceY(g26,g26) = 0.278384
    c: DistanceX(g26,g0) = 15.24
    c: Coincident(g28,g9)
    c: DistanceX(g5,g5) = 15.24
    c: DistanceX(g4,g4) = 13.208
    c: DistanceY(g23,g33) = 2.794
    c: Radius(g11) = 0.828548
FEATURE [Sketcher::SketchObject] Sketch010  label="DSub_single002"
  AttachmentOffset = pos=(0,0,0) rot=(0,0,1;1.5708rad)
  FullyConstrained = false
  MapMode = 45
  Placement = pos=(51.8643,-77.0142,71.9309) rot=(0,0,1;3.14159rad)
  Support = -> [BaseFeature]
  expr: .Placement.Base.z = 2.83
  sketch-geometry (44):
    g0: LineSegment StartX=0.8871 StartY=0.0324575 StartZ=0 EndX=29.8834 EndY=0.0324575 EndZ=0
    g1: LineSegment StartX=30.7903 StartY=-0.87451 StartZ=0 EndX=30.7903 EndY=-11.659 EndZ=0
    g2: LineSegment StartX=29.8834 StartY=-12.5659 StartZ=0 EndX=0.8871 EndY=-12.5659 EndZ=0
    g3: LineSegment StartX=-0.0198673 StartY=-11.659 StartZ=0 EndX=-0.0198673 EndY=-0.87451 EndZ=0
    g4: LineSegment StartX=9.03056 StartY=-0.245927 StartZ=0 EndX=21.7399 EndY=-0.245927 EndZ=0
    g5: LineSegment StartX=22.7172 StartY=-12.2876 StartZ=0 EndX=8.05325 EndY=-12.2876 EndZ=0
    g6: LineSegment StartX=6.62223 StartY=-2.11273 StartZ=0 EndX=5.22523 EndY=-9.60357 EndZ=0
    g7: LineSegment StartX=24.1482 StartY=-2.11273 StartZ=0 EndX=25.5452 EndY=-9.60357 EndZ=0
    g8: Circle CenterX=2.88843 CenterY=-6.26674 CenterZ=0 NormalX=0 NormalY=0 NormalZ=1 AngleXU=0 Radius=1.1303
    g9: Circle CenterX=27.882 CenterY=-6.26674 CenterZ=0 NormalX=0 NormalY=0 NormalZ=1 AngleXU=0 Radius=1.1303
    g10: ArcOfCircle CenterX=0.8871 CenterY=-0.87451 CenterZ=0 NormalX=0 NormalY=0 NormalZ=1 AngleXU=0 Radius=0.906967 StartAngle=1.5708 EndAngle=3.14159
    g11: ArcOfCircle CenterX=29.8834 CenterY=-0.87451 CenterZ=0 NormalX=0 NormalY=0 NormalZ=1 AngleXU=0 Radius=0.906967 StartAngle=0 EndAngle=1.5708
    g12: ArcOfCircle CenterX=29.8834 CenterY=-11.659 CenterZ=0 NormalX=0 NormalY=0 NormalZ=1 AngleXU=0 Radius=0.906967 StartAngle=4.71239 EndAngle=6.28319
    g13: ArcOfCircle CenterX=23.0052 CenterY=-9.75907 CenterZ=0 NormalX=0 NormalY=0 NormalZ=1 AngleXU=0 Radius=2.54483 StartAngle=4.599 EndAngle=6.34433
    g14: ArcOfCircle CenterX=7.76531 CenterY=-9.75907 CenterZ=0 NormalX=0 NormalY=0 NormalZ=1 AngleXU=0 Radius=2.54483 StartAngle=3.08045 EndAngle=4.82578
    g15: ArcOfCircle CenterX=9.04283 CenterY=-2.74862 CenterZ=0 NormalX=0 NormalY=0 NormalZ=1 AngleXU=0 Radius=2.50273 StartAngle=1.5757 EndAngle=2.88469
    g16: ArcOfCircle CenterX=21.7276 CenterY=-2.74862 CenterZ=0 NormalX=0 NormalY=0 NormalZ=1 AngleXU=0 Radius=2.50273 StartAngle=0.256898 EndAngle=1.5659
    g17: ArcOfCircle CenterX=0.8871 CenterY=-11.659 CenterZ=0 NormalX=0 NormalY=0 NormalZ=1 AngleXU=0 Radius=0.906967 StartAngle=3.14159 EndAngle=4.71239
    g18: LineSegment StartX=29.8834 StartY=0.0324575 StartZ=0 EndX=29.8834 EndY=-0.87451 EndZ=0
    g19: LineSegment StartX=29.8834 StartY=-0.87451 StartZ=0 EndX=30.7903 EndY=-0.87451 EndZ=0
    g20: LineSegment StartX=2.88843 StartY=-6.26674 StartZ=0 EndX=-0.0198673 EndY=-6.26674 EndZ=0
    g21: LineSegment StartX=27.882 StartY=-6.26674 StartZ=0 EndX=30.7903 EndY=-6.26674 EndZ=0
    g22: LineSegment StartX=2.88843 StartY=-6.26674 StartZ=0 EndX=2.88843 EndY=-12.5659 EndZ=0
    g23: LineSegment StartX=27.882 StartY=-6.26674 StartZ=0 EndX=27.882 EndY=-12.5659 EndZ=0
    g24: LineSegment StartX=2.88843 StartY=-6.26674 StartZ=0 EndX=2.88843 EndY=0.0324575 EndZ=0
    g25: LineSegment StartX=27.882 StartY=-6.26674 StartZ=0 EndX=27.882 EndY=0.0324575 EndZ=0
    g26: LineSegment StartX=2.88843 StartY=-6.26674 StartZ=0 EndX=27.882 EndY=-6.26674 EndZ=0
    g27: LineSegment StartX=14.6434 StartY=0.0324575 StartZ=0 EndX=14.6434 EndY=-0.245927 EndZ=0
    g28: LineSegment StartX=14.6434 StartY=-12.2876 StartZ=0 EndX=14.6434 EndY=-12.5659 EndZ=0
    g29: LineSegment StartX=24.9229 StartY=-6.26674 StartZ=0 EndX=26.7517 EndY=-6.26674 EndZ=0
    g30: LineSegment StartX=5.84753 StartY=-6.26674 StartZ=0 EndX=2.88843 EndY=-6.26674 EndZ=0
    g31: LineSegment StartX=6.62223 StartY=-2.11273 StartZ=0 EndX=-0.0198673 EndY=-2.11273 EndZ=0
    g32: LineSegment StartX=5.22523 StartY=-9.60357 StartZ=0 EndX=-0.0198673 EndY=-9.60357 EndZ=0
    g33: LineSegment StartX=24.1482 StartY=-2.11273 StartZ=0 EndX=30.7903 EndY=-2.11273 EndZ=0
    g34: LineSegment StartX=25.5452 StartY=-9.60357 StartZ=0 EndX=30.7903 EndY=-9.60357 EndZ=0
    g35: GeomPoint X=4.01873 Y=-6.26674 Z=0
    g36: LineSegment StartX=-0.0198673 StartY=-0.87451 StartZ=0 EndX=0.8871 EndY=-0.87451 EndZ=0
    g37: LineSegment StartX=0.8871 StartY=-0.87451 StartZ=0 EndX=0.8871 EndY=0.0324575 EndZ=0
    g38: LineSegment StartX=0.8871 StartY=-12.5659 StartZ=0 EndX=0.8871 EndY=-11.659 EndZ=0
    g39: LineSegment StartX=0.8871 StartY=-11.659 StartZ=0 EndX=-0.0198673 EndY=-11.659 EndZ=0
    g40: LineSegment StartX=29.8834 StartY=-12.5659 StartZ=0 EndX=29.8834 EndY=-11.659 EndZ=0
    g41: LineSegment StartX=29.8834 StartY=-11.659 StartZ=0 EndX=30.7903 EndY=-11.659 EndZ=0
    g42: LineSegment StartX=9.03056 StartY=-0.245927 StartZ=0 EndX=8.05325 EndY=-12.2876 EndZ=0
    g43: LineSegment StartX=21.7399 StartY=-0.245927 StartZ=0 EndX=22.7172 EndY=-12.2876 EndZ=0
  constraints (129):
    c: Equal(g7,g6)
    c: Coincident(g10,g3)
    c: Coincident(g10,g0)
    c: Coincident(g11,g0)
    c: Coincident(g11,g1)
    c: Coincident(g12,g1)
    c: Coincident(g12,g2)
    c: Coincident(g13,g7)
    c: Coincident(g13,g5)
    c: Coincident(g14,g6)
    c: Coincident(g14,g5)
    c: Coincident(g15,g6)
    c: Coincident(g15,g4)
    c: Coincident(g16,g4)
    c: Coincident(g16,g7)
    c: Coincident(g17,g2)
    c: Coincident(g17,g3)
    c: Equal(g8,g9)
    c: Diameter(g8) = 2.2606
    c: DistanceX(g8,g9) = 24.9936
    c: DistanceX(g3,g1) = 30.8102
    c: Parallel(g5,g2)
    c: Parallel(g2,g4)
    c: Parallel(g4,g0)
    c: Parallel(g1,g3)
    c: Perpendicular(g1,g0)
    c: Coincident(g18,g0)
    c: Coincident(g18,g11)
    c: Vertical(g18)
    c: Coincident(g19,g11)
    c: Coincident(g19,g1)
    c: Horizontal(g19)
    c: Vertical(g11,g12)
    c: Vertical(g12,g2)
    c: Horizontal(g1,g12)
    c: Horizontal(g12,g17)
    c: Horizontal(g17,g3)
    c: Vertical(g2,g17)
    c: Vertical(g17,g10)
    c: Vertical(g10,g0)
    c: Horizontal(g3,g10)
    c: Horizontal(g10,g11)
    c: DistanceY(g2,g0) = 12.5984
    c: Coincident(g20,g8)
    c: PointOnObject(g20,g3)
    c: Horizontal(g20)
    c: Coincident(g21,g9)
    c: PointOnObject(g21,g1)
    c: Horizontal(g21)
    c: Equal(g21,g20)
    c: Coincident(g22,g8)
    c: PointOnObject(g22,g2)
    c: Vertical(g22)
    c: Coincident(g23,g9)
    c: PointOnObject(g23,g2)
    c: Vertical(g23)
    c: Coincident(g24,g8)
    c: PointOnObject(g24,g0)
    c: Vertical(g24)
    c: Coincident(g25,g9)
    c: PointOnObject(g25,g0)
    c: Vertical(g25)
    c: Equal(g25,g24)
    c: Equal(g25,g23)
    c: Horizontal(g6,g7)
    c: Horizontal(g7,g6)
    c: PointOnObject(g27,g0)
    c: PointOnObject(g27,g4)
    c: Vertical(g27)
    c: PointOnObject(g28,g5)
    c: PointOnObject(g28,g2)
    c: Equal(g28,g27)
    c: Vertical(g28,g28)
    c: Vertical(g27,g28)
    c: PointOnObject(g29,g7)
    c: PointOnObject(g29,g26)
    c: Horizontal(g29)
    c: PointOnObject(g30,g6)
    c: Coincident(g30,g8)
    c: Horizontal(g30)
    c: Coincident(g26,g8)
    c: Equal(g16,g15)
    c: Equal(g14,g13)
    c: Angle(g16) = 1.309
    c: Angle(g13) = 1.74533
    c: Coincident(g31,g6)
    c: PointOnObject(g31,g3)
    c: Horizontal(g31)
    c: Coincident(g32,g6)
    c: PointOnObject(g32,g3)
    c: Horizontal(g32)
    c: Coincident(g33,g7)
    c: PointOnObject(g33,g1)
    c: Horizontal(g33)
    c: Coincident(g34,g7)
    c: PointOnObject(g34,g1)
    c: Horizontal(g34)
    c: Equal(g34,g32)
    c: PointOnObject(g35,g8)
    c: DistanceX(g35,g30) = 1.8288
    c: DistanceX(g29,g29) = 1.8288
    c: Horizontal(g8,g35)
    c: Angle(g15) = 1.309
    c: Angle(g14) = 1.74533
    c: DistanceX(g6,g7) = 17.526
    c: DistanceX(g6,g7) = 20.32
    c: DistanceX(g20,g30) = 5.8674
    c: DistanceX(g29,g21) = 5.8674
    c: Coincident(g26,g9)
    c: Distance(g7) = 7.62
    c: Coincident(g36,g3)
    c: Coincident(g36,g10)
    c: Coincident(g37,g10)
    c: Coincident(g37,g0)
    c: Coincident(g38,g2)
    c: Coincident(g38,g17)
    c: Coincident(g39,g17)
    c: Coincident(g39,g3)
    c: Coincident(g40,g2)
    c: Coincident(g40,g12)
    c: Coincident(g41,g12)
    c: Coincident(g41,g1)
    c: Coincident(g42,g4)
    c: Coincident(g42,g5)
    c: Coincident(g43,g4)
    c: Coincident(g43,g5)
    c: Angle(g42,g26) = 1.65178
    c: DistanceY(g27,g27) = 0.278384
    c: DistanceX(g27,g0) = 15.24
FEATURE [Sketcher::SketchObject] Sketch011  label="DSubs"
  AttachmentOffset = pos=(228.6,-152.4,0) rot=(0,0,1;3.14159rad)
  ExternalGeometry = -> [DatumLine001,DatumLine]
  FullyConstrained = true
  MapMode = 5
  Placement = pos=(228.6,-152.4,71.9309) rot=(0,0,1;3.14159rad)
  Support = -> [BaseFeature]
  expr: Constraints[100] = Sketch009.Constraints[100]
  expr: Constraints[101] = Sketch009.Constraints[101]
  expr: Constraints[104] = Sketch009.Constraints[104]
  expr: Constraints[121] = Sketch009.Constraints[121]
  expr: Constraints[122] = Sketch009.Constraints[122]
  expr: Constraints[124] = Sketch009.Constraints[124]
  expr: Constraints[125] = Sketch009.Constraints[125]
  expr: Constraints[126] = Sketch009.Constraints[126]
  expr: Constraints[127] = Sketch009.Constraints[127]
  expr: Constraints[146] = Sketch009.Constraints[18]
  expr: Constraints[147] = Sketch009.Constraints[19]
  expr: Constraints[148] = Sketch009.Constraints[20]
  expr: Constraints[170] = Sketch009.Constraints[42]
  expr: Constraints[18] = Sketch009.Constraints[18]
  expr: Constraints[19] = Sketch009.Constraints[19]
  expr: Constraints[209] = Sketch009.Constraints[81]
  expr: Constraints[20] = Sketch009.Constraints[20]
  expr: Constraints[210] = Sketch009.Constraints[82]
  expr: Constraints[226] = Sketch009.Constraints[98]
  expr: Constraints[227] = Sketch009.Constraints[99]
  expr: Constraints[228] = Sketch009.Constraints[100]
  expr: Constraints[229] = Sketch009.Constraints[101]
  expr: Constraints[232] = Sketch009.Constraints[104]
  expr: Constraints[249] = Sketch009.Constraints[121]
  expr: Constraints[250] = Sketch009.Constraints[122]
  expr: Constraints[252] = Sketch009.Constraints[124]
  expr: Constraints[253] = Sketch009.Constraints[125]
  expr: Constraints[254] = Sketch009.Constraints[126]
  expr: Constraints[255] = Sketch009.Constraints[127]
  expr: Constraints[274] = Sketch009.Constraints[18]
  expr: Constraints[275] = Sketch009.Constraints[19]
  expr: Constraints[276] = Sketch009.Constraints[20]
  expr: Constraints[298] = Sketch009.Constraints[42]
  expr: Constraints[337] = Sketch009.Constraints[81]
  expr: Constraints[338] = Sketch009.Constraints[82]
  expr: Constraints[354] = Sketch009.Constraints[98]
  expr: Constraints[355] = Sketch009.Constraints[99]
  expr: Constraints[356] = Sketch009.Constraints[100]
  expr: Constraints[357] = Sketch009.Constraints[101]
  expr: Constraints[360] = Sketch009.Constraints[104]
  expr: Constraints[377] = Sketch009.Constraints[121]
  expr: Constraints[378] = Sketch009.Constraints[122]
  expr: Constraints[380] = Sketch009.Constraints[124]
  expr: Constraints[381] = Sketch009.Constraints[125]
  expr: Constraints[382] = Sketch009.Constraints[126]
  expr: Constraints[383] = Sketch009.Constraints[127]
  expr: Constraints[402] = Sketch009.Constraints[18]
  expr: Constraints[403] = Sketch009.Constraints[19]
  expr: Constraints[404] = Sketch009.Constraints[20]
  expr: Constraints[426] = Sketch009.Constraints[42]
  expr: Constraints[42] = Sketch009.Constraints[42]
  expr: Constraints[465] = Sketch009.Constraints[81]
  expr: Constraints[466] = Sketch009.Constraints[82]
  expr: Constraints[482] = Sketch009.Constraints[98]
  expr: Constraints[483] = Sketch009.Constraints[99]
  expr: Constraints[484] = Sketch009.Constraints[100]
  expr: Constraints[485] = Sketch009.Constraints[101]
  expr: Constraints[488] = Sketch009.Constraints[104]
  expr: Constraints[505] = Sketch009.Constraints[121]
  expr: Constraints[506] = Sketch009.Constraints[122]
  expr: Constraints[508] = Sketch009.Constraints[124]
  expr: Constraints[509] = Sketch009.Constraints[125]
  expr: Constraints[510] = Sketch009.Constraints[126]
  expr: Constraints[511] = Sketch009.Constraints[127]
  expr: Constraints[81] = Sketch009.Constraints[81]
  expr: Constraints[82] = Sketch009.Constraints[82]
  expr: Constraints[98] = Sketch009.Constraints[98]
  expr: Constraints[99] = Sketch009.Constraints[99]
  sketch-geometry (176):
    g0: LineSegment StartX=124.262 StartY=-50.0874 StartZ=0 EndX=153.415 EndY=-50.0874 EndZ=0
    g1: LineSegment StartX=154.244 StartY=-50.916 StartZ=0 EndX=154.244 EndY=-61.8573 EndZ=0
    g2: LineSegment StartX=153.415 StartY=-62.6858 StartZ=0 EndX=124.262 EndY=-62.6858 EndZ=0
    g3: LineSegment StartX=123.434 StartY=-61.8573 StartZ=0 EndX=123.434 EndY=-50.916 EndZ=0
    g4: LineSegment StartX=132.235 StartY=-50.3658 StartZ=0 EndX=145.443 EndY=-50.3658 EndZ=0
    g5: LineSegment StartX=146.459 StartY=-62.4074 StartZ=0 EndX=131.219 EndY=-62.4074 EndZ=0
    g6: LineSegment StartX=130.076 StartY=-52.401 StartZ=0 EndX=128.679 EndY=-59.8918 EndZ=0
    g7: LineSegment StartX=147.602 StartY=-52.401 StartZ=0 EndX=148.999 EndY=-59.8918 EndZ=0
    g8: Circle CenterX=126.342 CenterY=-56.3866 CenterZ=0 NormalX=0 NormalY=0 NormalZ=1 AngleXU=0 Radius=1.1303
    g9: Circle CenterX=151.336 CenterY=-56.3866 CenterZ=0 NormalX=0 NormalY=0 NormalZ=1 AngleXU=0 Radius=1.1303
    g10: ArcOfCircle CenterX=124.262 CenterY=-50.916 CenterZ=0 NormalX=0 NormalY=0 NormalZ=1 AngleXU=0 Radius=0.828548 StartAngle=1.5708 EndAngle=3.14159
    g11: ArcOfCircle CenterX=153.415 CenterY=-50.916 CenterZ=0 NormalX=0 NormalY=0 NormalZ=1 AngleXU=0 Radius=0.828548 StartAngle=0 EndAngle=1.5708
    g12: ArcOfCircle CenterX=153.415 CenterY=-61.8573 CenterZ=0 NormalX=0 NormalY=0 NormalZ=1 AngleXU=0 Radius=0.828548 StartAngle=4.71239 EndAngle=6.28319
    g13: ArcOfCircle CenterX=146.674 CenterY=-60.084 CenterZ=0 NormalX=0 NormalY=0 NormalZ=1 AngleXU=0 Radius=2.33335 StartAngle=4.6203 EndAngle=6.36563
    g14: ArcOfCircle CenterX=131.004 CenterY=-60.084 CenterZ=0 NormalX=0 NormalY=0 NormalZ=1 AngleXU=0 Radius=2.33335 StartAngle=3.05915 EndAngle=4.80448
    g15: ArcOfCircle CenterX=132.482 CenterY=-52.7902 CenterZ=0 NormalX=0 NormalY=0 NormalZ=1 AngleXU=0 Radius=2.43693 StartAngle=1.67218 EndAngle=2.98118
    g16: ArcOfCircle CenterX=145.196 CenterY=-52.7902 CenterZ=0 NormalX=0 NormalY=0 NormalZ=1 AngleXU=0 Radius=2.43693 StartAngle=0.160416 EndAngle=1.46941
    g17: ArcOfCircle CenterX=124.262 CenterY=-61.8573 CenterZ=0 NormalX=0 NormalY=0 NormalZ=1 AngleXU=0 Radius=0.828548 StartAngle=3.14159 EndAngle=4.71239
    g18: LineSegment StartX=153.415 StartY=-50.0874 StartZ=0 EndX=153.415 EndY=-50.916 EndZ=0
    g19: LineSegment StartX=153.415 StartY=-50.916 StartZ=0 EndX=154.244 EndY=-50.916 EndZ=0
    g20: LineSegment StartX=126.342 StartY=-56.3866 StartZ=0 EndX=123.434 EndY=-56.3866 EndZ=0
    g21: LineSegment StartX=151.336 StartY=-56.3866 StartZ=0 EndX=154.244 EndY=-56.3866 EndZ=0
    g22: LineSegment StartX=126.342 StartY=-56.3866 StartZ=0 EndX=126.342 EndY=-62.6858 EndZ=0
    g23: LineSegment StartX=151.336 StartY=-56.3866 StartZ=0 EndX=151.336 EndY=-62.6858 EndZ=0
    g24: LineSegment StartX=126.342 StartY=-56.3866 StartZ=0 EndX=126.342 EndY=-50.0874 EndZ=0
    g25: LineSegment StartX=151.336 StartY=-56.3866 StartZ=0 EndX=151.336 EndY=-50.0874 EndZ=0
    g26: LineSegment StartX=138.175 StartY=-50.0874 StartZ=0 EndX=138.175 EndY=-50.3658 EndZ=0
    g27: LineSegment StartX=138.175 StartY=-62.4074 StartZ=0 EndX=138.175 EndY=-62.6858 EndZ=0
    g28: LineSegment StartX=148.345 StartY=-56.3866 StartZ=0 EndX=151.336 EndY=-56.3866 EndZ=0
    g29: LineSegment StartX=129.333 StartY=-56.3866 StartZ=0 EndX=126.342 EndY=-56.3866 EndZ=0
    g30: LineSegment StartX=130.076 StartY=-52.401 StartZ=0 EndX=123.434 EndY=-52.401 EndZ=0
    g31: LineSegment StartX=128.679 StartY=-59.8918 StartZ=0 EndX=123.434 EndY=-59.8918 EndZ=0
    g32: LineSegment StartX=147.602 StartY=-52.401 StartZ=0 EndX=154.244 EndY=-52.401 EndZ=0
    g33: LineSegment StartX=148.999 StartY=-59.8918 StartZ=0 EndX=154.244 EndY=-59.8918 EndZ=0
    g34: GeomPoint X=127.472 Y=-56.3866 Z=0
    g35: LineSegment StartX=123.434 StartY=-50.916 StartZ=0 EndX=124.262 EndY=-50.916 EndZ=0
    g36: LineSegment StartX=124.262 StartY=-50.916 StartZ=0 EndX=124.262 EndY=-50.0874 EndZ=0
    g37: LineSegment StartX=124.262 StartY=-62.6858 StartZ=0 EndX=124.262 EndY=-61.8573 EndZ=0
    g38: LineSegment StartX=124.262 StartY=-61.8573 StartZ=0 EndX=123.434 EndY=-61.8573 EndZ=0
    g39: LineSegment StartX=153.415 StartY=-62.6858 StartZ=0 EndX=153.415 EndY=-61.8573 EndZ=0
    g40: LineSegment StartX=153.415 StartY=-61.8573 StartZ=0 EndX=154.244 EndY=-61.8573 EndZ=0
    g41: LineSegment StartX=132.235 StartY=-50.3658 StartZ=0 EndX=131.219 EndY=-62.4074 EndZ=0
    g42: LineSegment StartX=145.443 StartY=-50.3658 StartZ=0 EndX=146.459 EndY=-62.4074 EndZ=0
    g43: LineSegment StartX=124.262 StartY=-88.0858 StartZ=0 EndX=153.415 EndY=-88.0858 EndZ=0
    g44: LineSegment StartX=154.244 StartY=-88.9144 StartZ=0 EndX=154.244 EndY=-99.8557 EndZ=0
    g45: LineSegment StartX=153.415 StartY=-100.684 StartZ=0 EndX=124.262 EndY=-100.684 EndZ=0
    g46: LineSegment StartX=123.434 StartY=-99.8557 StartZ=0 EndX=123.434 EndY=-88.9144 EndZ=0
    g47: LineSegment StartX=132.235 StartY=-88.3642 StartZ=0 EndX=145.443 EndY=-88.3642 EndZ=0
    g48: LineSegment StartX=146.459 StartY=-100.406 StartZ=0 EndX=131.219 EndY=-100.406 EndZ=0
    g49: LineSegment StartX=130.076 StartY=-90.3994 StartZ=0 EndX=128.679 EndY=-97.8902 EndZ=0
    g50: LineSegment StartX=147.602 StartY=-90.3994 StartZ=0 EndX=148.999 EndY=-97.8902 EndZ=0
    g51: Circle CenterX=126.342 CenterY=-94.385 CenterZ=0 NormalX=0 NormalY=0 NormalZ=1 AngleXU=0 Radius=1.1303
    g52: Circle CenterX=151.336 CenterY=-94.385 CenterZ=0 NormalX=0 NormalY=0 NormalZ=1 AngleXU=0 Radius=1.1303
    g53: ArcOfCircle CenterX=124.262 CenterY=-88.9144 CenterZ=0 NormalX=0 NormalY=0 NormalZ=1 AngleXU=0 Radius=0.828548 StartAngle=1.5708 EndAngle=3.14159
    g54: ArcOfCircle CenterX=153.415 CenterY=-88.9144 CenterZ=0 NormalX=0 NormalY=0 NormalZ=1 AngleXU=0 Radius=0.828548 StartAngle=0 EndAngle=1.5708
    g55: ArcOfCircle CenterX=153.415 CenterY=-99.8557 CenterZ=0 NormalX=0 NormalY=0 NormalZ=1 AngleXU=0 Radius=0.828548 StartAngle=4.71239 EndAngle=6.28319
    g56: ArcOfCircle CenterX=146.674 CenterY=-98.0824 CenterZ=0 NormalX=0 NormalY=0 NormalZ=1 AngleXU=0 Radius=2.33335 StartAngle=4.6203 EndAngle=6.36563
    g57: ArcOfCircle CenterX=131.004 CenterY=-98.0824 CenterZ=0 NormalX=0 NormalY=0 NormalZ=1 AngleXU=0 Radius=2.33335 StartAngle=3.05915 EndAngle=4.80448
    g58: ArcOfCircle CenterX=132.482 CenterY=-90.7886 CenterZ=0 NormalX=0 NormalY=0 NormalZ=1 AngleXU=0 Radius=2.43693 StartAngle=1.67218 EndAngle=2.98118
    g59: ArcOfCircle CenterX=145.196 CenterY=-90.7886 CenterZ=0 NormalX=0 NormalY=0 NormalZ=1 AngleXU=0 Radius=2.43693 StartAngle=0.160416 EndAngle=1.46941
    g60: ArcOfCircle CenterX=124.262 CenterY=-99.8557 CenterZ=0 NormalX=0 NormalY=0 NormalZ=1 AngleXU=0 Radius=0.828548 StartAngle=3.14159 EndAngle=4.71239
    g61: LineSegment StartX=153.415 StartY=-88.0858 StartZ=0 EndX=153.415 EndY=-88.9144 EndZ=0
    g62: LineSegment StartX=153.415 StartY=-88.9144 StartZ=0 EndX=154.244 EndY=-88.9144 EndZ=0
    g63: LineSegment StartX=126.342 StartY=-94.385 StartZ=0 EndX=123.434 EndY=-94.385 EndZ=0
    g64: LineSegment StartX=151.336 StartY=-94.385 StartZ=0 EndX=154.244 EndY=-94.385 EndZ=0
    g65: LineSegment StartX=126.342 StartY=-94.385 StartZ=0 EndX=126.342 EndY=-100.684 EndZ=0
    g66: LineSegment StartX=151.336 StartY=-94.385 StartZ=0 EndX=151.336 EndY=-100.684 EndZ=0
    g67: LineSegment StartX=126.342 StartY=-94.385 StartZ=0 EndX=126.342 EndY=-88.0858 EndZ=0
    g68: LineSegment StartX=151.336 StartY=-94.385 StartZ=0 EndX=151.336 EndY=-88.0858 EndZ=0
    g69: LineSegment StartX=138.175 StartY=-88.0858 StartZ=0 EndX=138.175 EndY=-88.3642 EndZ=0
    g70: LineSegment StartX=138.175 StartY=-100.406 StartZ=0 EndX=138.175 EndY=-100.684 EndZ=0
    g71: LineSegment StartX=148.345 StartY=-94.385 StartZ=0 EndX=151.336 EndY=-94.385 EndZ=0
    g72: LineSegment StartX=129.333 StartY=-94.385 StartZ=0 EndX=126.342 EndY=-94.385 EndZ=0
    g73: LineSegment StartX=130.076 StartY=-90.3994 StartZ=0 EndX=123.434 EndY=-90.3994 EndZ=0
    g74: LineSegment StartX=128.679 StartY=-97.8902 StartZ=0 EndX=123.434 EndY=-97.8902 EndZ=0
    g75: LineSegment StartX=147.602 StartY=-90.3994 StartZ=0 EndX=154.244 EndY=-90.3994 EndZ=0
    g76: LineSegment StartX=148.999 StartY=-97.8902 StartZ=0 EndX=154.244 EndY=-97.8902 EndZ=0
    g77: GeomPoint X=127.472 Y=-94.385 Z=0
    g78: LineSegment StartX=123.434 StartY=-88.9144 StartZ=0 EndX=124.262 EndY=-88.9144 EndZ=0
    g79: LineSegment StartX=124.262 StartY=-88.9144 StartZ=0 EndX=124.262 EndY=-88.0858 EndZ=0
    g80: LineSegment StartX=124.262 StartY=-100.684 StartZ=0 EndX=124.262 EndY=-99.8557 EndZ=0
    g81: LineSegment StartX=124.262 StartY=-99.8557 StartZ=0 EndX=123.434 EndY=-99.8557 EndZ=0
    g82: LineSegment StartX=153.415 StartY=-100.684 StartZ=0 EndX=153.415 EndY=-99.8557 EndZ=0
    g83: LineSegment StartX=153.415 StartY=-99.8557 StartZ=0 EndX=154.244 EndY=-99.8557 EndZ=0
    g84: LineSegment StartX=132.235 StartY=-88.3642 StartZ=0 EndX=131.219 EndY=-100.406 EndZ=0
    g85: LineSegment StartX=145.443 StartY=-88.3642 StartZ=0 EndX=146.459 EndY=-100.406 EndZ=0
    g86: LineSegment StartX=73.8688 StartY=-88.0858 StartZ=0 EndX=103.022 EndY=-88.0858 EndZ=0
    g87: LineSegment StartX=103.85 StartY=-88.9144 StartZ=0 EndX=103.85 EndY=-99.8557 EndZ=0
    g88: LineSegment StartX=103.022 StartY=-100.684 StartZ=0 EndX=73.8688 EndY=-100.684 EndZ=0
    g89: LineSegment StartX=73.0402 StartY=-99.8557 StartZ=0 EndX=73.0402 EndY=-88.9144 EndZ=0
    g90: LineSegment StartX=81.8413 StartY=-88.3642 StartZ=0 EndX=95.0493 EndY=-88.3642 EndZ=0
    g91: LineSegment StartX=96.0653 StartY=-100.406 StartZ=0 EndX=80.8253 EndY=-100.406 EndZ=0
    g92: LineSegment StartX=79.6823 StartY=-90.3994 StartZ=0 EndX=78.2853 EndY=-97.8902 EndZ=0
    g93: LineSegment StartX=97.2083 StartY=-90.3994 StartZ=0 EndX=98.6053 EndY=-97.8902 EndZ=0
    g94: Circle CenterX=75.9485 CenterY=-94.385 CenterZ=0 NormalX=0 NormalY=0 NormalZ=1 AngleXU=0 Radius=1.1303
    g95: Circle CenterX=100.942 CenterY=-94.385 CenterZ=0 NormalX=0 NormalY=0 NormalZ=1 AngleXU=0 Radius=1.1303
    g96: ArcOfCircle CenterX=73.8688 CenterY=-88.9144 CenterZ=0 NormalX=0 NormalY=0 NormalZ=1 AngleXU=0 Radius=0.828548 StartAngle=1.5708 EndAngle=3.14159
    g97: ArcOfCircle CenterX=103.022 CenterY=-88.9144 CenterZ=0 NormalX=0 NormalY=0 NormalZ=1 AngleXU=0 Radius=0.828548 StartAngle=0 EndAngle=1.5708
    g98: ArcOfCircle CenterX=103.022 CenterY=-99.8557 CenterZ=0 NormalX=0 NormalY=0 NormalZ=1 AngleXU=0 Radius=0.828548 StartAngle=4.71239 EndAngle=6.28319
    g99: ArcOfCircle CenterX=96.2799 CenterY=-98.0824 CenterZ=0 NormalX=0 NormalY=0 NormalZ=1 AngleXU=0 Radius=2.33335 StartAngle=4.6203 EndAngle=6.36563
    g100: ArcOfCircle CenterX=80.6108 CenterY=-98.0824 CenterZ=0 NormalX=0 NormalY=0 NormalZ=1 AngleXU=0 Radius=2.33335 StartAngle=3.05915 EndAngle=4.80448
    g101: ArcOfCircle CenterX=82.088 CenterY=-90.7886 CenterZ=0 NormalX=0 NormalY=0 NormalZ=1 AngleXU=0 Radius=2.43693 StartAngle=1.67218 EndAngle=2.98118
    g102: ArcOfCircle CenterX=94.8027 CenterY=-90.7886 CenterZ=0 NormalX=0 NormalY=0 NormalZ=1 AngleXU=0 Radius=2.43693 StartAngle=0.160416 EndAngle=1.46941
    g103: ArcOfCircle CenterX=73.8688 CenterY=-99.8557 CenterZ=0 NormalX=0 NormalY=0 NormalZ=1 AngleXU=0 Radius=0.828548 StartAngle=3.14159 EndAngle=4.71239
    g104: LineSegment StartX=103.022 StartY=-88.0858 StartZ=0 EndX=103.022 EndY=-88.9144 EndZ=0
    g105: LineSegment StartX=103.022 StartY=-88.9144 StartZ=0 EndX=103.85 EndY=-88.9144 EndZ=0
    g106: LineSegment StartX=75.9485 StartY=-94.385 StartZ=0 EndX=73.0402 EndY=-94.385 EndZ=0
    g107: LineSegment StartX=100.942 StartY=-94.385 StartZ=0 EndX=103.85 EndY=-94.385 EndZ=0
    g108: LineSegment StartX=75.9485 StartY=-94.385 StartZ=0 EndX=75.9485 EndY=-100.684 EndZ=0
    g109: LineSegment StartX=100.942 StartY=-94.385 StartZ=0 EndX=100.942 EndY=-100.684 EndZ=0
    g110: LineSegment StartX=75.9485 StartY=-94.385 StartZ=0 EndX=75.9485 EndY=-88.0858 EndZ=0
    g111: LineSegment StartX=100.942 StartY=-94.385 StartZ=0 EndX=100.942 EndY=-88.0858 EndZ=0
    g112: LineSegment StartX=87.7819 StartY=-88.0858 StartZ=0 EndX=87.7819 EndY=-88.3642 EndZ=0
    g113: LineSegment StartX=87.7819 StartY=-100.406 StartZ=0 EndX=87.7819 EndY=-100.684 EndZ=0
    g114: LineSegment StartX=97.9516 StartY=-94.385 StartZ=0 EndX=100.942 EndY=-94.385 EndZ=0
    g115: LineSegment StartX=78.939 StartY=-94.385 StartZ=0 EndX=75.9485 EndY=-94.385 EndZ=0
    g116: LineSegment StartX=79.6823 StartY=-90.3994 StartZ=0 EndX=73.0402 EndY=-90.3994 EndZ=0
    g117: LineSegment StartX=78.2853 StartY=-97.8902 StartZ=0 EndX=73.0402 EndY=-97.8902 EndZ=0
    g118: LineSegment StartX=97.2083 StartY=-90.3994 StartZ=0 EndX=103.85 EndY=-90.3994 EndZ=0
    g119: LineSegment StartX=98.6053 StartY=-97.8902 StartZ=0 EndX=103.85 EndY=-97.8902 EndZ=0
    g120: GeomPoint X=77.0788 Y=-94.385 Z=0
    g121: LineSegment StartX=73.0402 StartY=-88.9144 StartZ=0 EndX=73.8688 EndY=-88.9144 EndZ=0
    g122: LineSegment StartX=73.8688 StartY=-88.9144 StartZ=0 EndX=73.8688 EndY=-88.0858 EndZ=0
    g123: LineSegment StartX=73.8688 StartY=-100.684 StartZ=0 EndX=73.8688 EndY=-99.8557 EndZ=0
    g124: LineSegment StartX=73.8688 StartY=-99.8557 StartZ=0 EndX=73.0402 EndY=-99.8557 EndZ=0
    g125: LineSegment StartX=103.022 StartY=-100.684 StartZ=0 EndX=103.022 EndY=-99.8557 EndZ=0
    g126: LineSegment StartX=103.022 StartY=-99.8557 StartZ=0 EndX=103.85 EndY=-99.8557 EndZ=0
    g127: LineSegment StartX=81.8413 StartY=-88.3642 StartZ=0 EndX=80.8253 EndY=-100.406 EndZ=0
    g128: LineSegment StartX=95.0493 StartY=-88.3642 StartZ=0 EndX=96.0653 EndY=-100.406 EndZ=0
    g129: LineSegment StartX=73.8688 StartY=-50.0874 StartZ=0 EndX=103.022 EndY=-50.0874 EndZ=0
    g130: LineSegment StartX=103.85 StartY=-50.916 StartZ=0 EndX=103.85 EndY=-61.8573 EndZ=0
    g131: LineSegment StartX=103.022 StartY=-62.6858 StartZ=0 EndX=73.8688 EndY=-62.6858 EndZ=0
    g132: LineSegment StartX=73.0402 StartY=-61.8573 StartZ=0 EndX=73.0402 EndY=-50.916 EndZ=0
    g133: LineSegment StartX=81.8413 StartY=-50.3658 StartZ=0 EndX=95.0493 EndY=-50.3658 EndZ=0
    g134: LineSegment StartX=96.0653 StartY=-62.4074 StartZ=0 EndX=80.8253 EndY=-62.4074 EndZ=0
    g135: LineSegment StartX=79.6823 StartY=-52.401 StartZ=0 EndX=78.2853 EndY=-59.8918 EndZ=0
    g136: LineSegment StartX=97.2083 StartY=-52.401 StartZ=0 EndX=98.6053 EndY=-59.8918 EndZ=0
    g137: Circle CenterX=75.9485 CenterY=-56.3866 CenterZ=0 NormalX=0 NormalY=0 NormalZ=1 AngleXU=0 Radius=1.1303
    g138: Circle CenterX=100.942 CenterY=-56.3866 CenterZ=0 NormalX=0 NormalY=0 NormalZ=1 AngleXU=0 Radius=1.1303
    g139: ArcOfCircle CenterX=73.8688 CenterY=-50.916 CenterZ=0 NormalX=0 NormalY=0 NormalZ=1 AngleXU=0 Radius=0.828548 StartAngle=1.5708 EndAngle=3.14159
    g140: ArcOfCircle CenterX=103.022 CenterY=-50.916 CenterZ=0 NormalX=0 NormalY=0 NormalZ=1 AngleXU=0 Radius=0.828548 StartAngle=0 EndAngle=1.5708
    g141: ArcOfCircle CenterX=103.022 CenterY=-61.8573 CenterZ=0 NormalX=0 NormalY=0 NormalZ=1 AngleXU=0 Radius=0.828548 StartAngle=4.71239 EndAngle=6.28319
    g142: ArcOfCircle CenterX=96.2799 CenterY=-60.084 CenterZ=0 NormalX=0 NormalY=0 NormalZ=1 AngleXU=0 Radius=2.33335 StartAngle=4.6203 EndAngle=6.36563
    g143: ArcOfCircle CenterX=80.6108 CenterY=-60.084 CenterZ=0 NormalX=0 NormalY=0 NormalZ=1 AngleXU=0 Radius=2.33335 StartAngle=3.05915 EndAngle=4.80448
    g144: ArcOfCircle CenterX=82.088 CenterY=-52.7902 CenterZ=0 NormalX=0 NormalY=0 NormalZ=1 AngleXU=0 Radius=2.43693 StartAngle=1.67218 EndAngle=2.98118
    g145: ArcOfCircle CenterX=94.8027 CenterY=-52.7902 CenterZ=0 NormalX=0 NormalY=0 NormalZ=1 AngleXU=0 Radius=2.43693 StartAngle=0.160416 EndAngle=1.46941
    g146: ArcOfCircle CenterX=73.8688 CenterY=-61.8573 CenterZ=0 NormalX=0 NormalY=0 NormalZ=1 AngleXU=0 Radius=0.828548 StartAngle=3.14159 EndAngle=4.71239
    g147: LineSegment StartX=103.022 StartY=-50.0874 StartZ=0 EndX=103.022 EndY=-50.916 EndZ=0
    g148: LineSegment StartX=103.022 StartY=-50.916 StartZ=0 EndX=103.85 EndY=-50.916 EndZ=0
    g149: LineSegment StartX=75.9485 StartY=-56.3866 StartZ=0 EndX=73.0402 EndY=-56.3866 EndZ=0
    g150: LineSegment StartX=100.942 StartY=-56.3866 StartZ=0 EndX=103.85 EndY=-56.3866 EndZ=0
    g151: LineSegment StartX=75.9485 StartY=-56.3866 StartZ=0 EndX=75.9485 EndY=-62.6858 EndZ=0
    g152: LineSegment StartX=100.942 StartY=-56.3866 StartZ=0 EndX=100.942 EndY=-62.6858 EndZ=0
    g153: LineSegment StartX=75.9485 StartY=-56.3866 StartZ=0 EndX=75.9485 EndY=-50.0874 EndZ=0
    g154: LineSegment StartX=100.942 StartY=-56.3866 StartZ=0 EndX=100.942 EndY=-50.0874 EndZ=0
    g155: LineSegment StartX=87.7819 StartY=-50.0874 StartZ=0 EndX=87.7819 EndY=-50.3658 EndZ=0
    g156: LineSegment StartX=87.7819 StartY=-62.4074 StartZ=0 EndX=87.7819 EndY=-62.6858 EndZ=0
    g157: LineSegment StartX=97.9516 StartY=-56.3866 StartZ=0 EndX=100.942 EndY=-56.3866 EndZ=0
    g158: LineSegment StartX=78.939 StartY=-56.3866 StartZ=0 EndX=75.9485 EndY=-56.3866 EndZ=0
    g159: LineSegment StartX=79.6823 StartY=-52.401 StartZ=0 EndX=73.0402 EndY=-52.401 EndZ=0
    g160: LineSegment StartX=78.2853 StartY=-59.8918 StartZ=0 EndX=73.0402 EndY=-59.8918 EndZ=0
    g161: LineSegment StartX=97.2083 StartY=-52.401 StartZ=0 EndX=103.85 EndY=-52.401 EndZ=0
    g162: LineSegment StartX=98.6053 StartY=-59.8918 StartZ=0 EndX=103.85 EndY=-59.8918 EndZ=0
    g163: GeomPoint X=77.0788 Y=-56.3866 Z=0
    g164: LineSegment StartX=73.0402 StartY=-50.916 StartZ=0 EndX=73.8688 EndY=-50.916 EndZ=0
    g165: LineSegment StartX=73.8688 StartY=-50.916 StartZ=0 EndX=73.8688 EndY=-50.0874 EndZ=0
    g166: LineSegment StartX=73.8688 StartY=-62.6858 StartZ=0 EndX=73.8688 EndY=-61.8573 EndZ=0
    g167: LineSegment StartX=73.8688 StartY=-61.8573 StartZ=0 EndX=73.0402 EndY=-61.8573 EndZ=0
    g168: LineSegment StartX=103.022 StartY=-62.6858 StartZ=0 EndX=103.022 EndY=-61.8573 EndZ=0
    g169: LineSegment StartX=103.022 StartY=-61.8573 StartZ=0 EndX=103.85 EndY=-61.8573 EndZ=0
    g170: LineSegment StartX=81.8413 StartY=-50.3658 StartZ=0 EndX=80.8253 EndY=-62.4074 EndZ=0
    g171: LineSegment StartX=95.0493 StartY=-50.3658 StartZ=0 EndX=96.0653 EndY=-62.4074 EndZ=0
    g172: LineSegment StartX=138.175 StartY=-88.0858 StartZ=0 EndX=138.175 EndY=-75.3858 EndZ=0
    g173: LineSegment StartX=138.175 StartY=-75.3858 StartZ=0 EndX=138.175 EndY=-62.6858 EndZ=0
    g174: LineSegment StartX=126.342 StartY=-56.3866 StartZ=0 EndX=100.942 EndY=-56.3866 EndZ=0
    g175: LineSegment StartX=151.336 StartY=-56.3866 StartZ=0 EndX=176.736 EndY=-56.3866 EndZ=0
  constraints (530):
    c: Equal(g7,g6)
    c: Coincident(g10,g3)
    c: Coincident(g10,g0)
    c: Coincident(g11,g0)
    c: Coincident(g11,g1)
    c: Coincident(g12,g1)
    c: Coincident(g12,g2)
    c: Coincident(g13,g7)
    c: Coincident(g13,g5)
    c: Coincident(g14,g6)
    c: Coincident(g14,g5)
    c: Coincident(g15,g6)
    c: Coincident(g15,g4)
    c: Coincident(g16,g4)
    c: Coincident(g16,g7)
    c: Coincident(g17,g2)
    c: Coincident(g17,g3)
    c: Equal(g8,g9)
    c: Diameter(g8) = 2.2606
    c: DistanceX(g8,g9) = 24.9936
    c: DistanceX(g3,g1) = 30.8102
    c: Parallel(g5,g2)
    c: Parallel(g2,g4)
    c: Parallel(g4,g0)
    c: Parallel(g1,g3)
    c: Perpendicular(g1,g0)
    c: Coincident(g18,g0)
    c: Coincident(g18,g11)
    c: Vertical(g18)
    c: Coincident(g19,g11)
    c: Coincident(g19,g1)
    c: Horizontal(g19)
    c: Vertical(g11,g12)
    c: Vertical(g12,g2)
    c: Horizontal(g1,g12)
    c: Horizontal(g12,g17)
    c: Horizontal(g17,g3)
    c: Vertical(g2,g17)
    c: Vertical(g17,g10)
    c: Vertical(g10,g0)
    c: Horizontal(g3,g10)
    c: Horizontal(g10,g11)
    c: DistanceY(g2,g0) = 12.5984
    c: Coincident(g20,g8)
    c: PointOnObject(g20,g3)
    c: Horizontal(g20)
    c: Coincident(g21,g9)
    c: PointOnObject(g21,g1)
    c: Horizontal(g21)
    c: Equal(g21,g20)
    c: Coincident(g22,g8)
    c: PointOnObject(g22,g2)
    c: Vertical(g22)
    c: Coincident(g23,g9)
    c: PointOnObject(g23,g2)
    c: Vertical(g23)
    c: Coincident(g24,g8)
    c: PointOnObject(g24,g0)
    c: Vertical(g24)
    c: Coincident(g25,g9)
    c: PointOnObject(g25,g0)
    c: Vertical(g25)
    c: Equal(g25,g24)
    c: Equal(g25,g23)
    c: Horizontal(g6,g7)
    c: Horizontal(g7,g6)
    c: PointOnObject(g26,g0)
    c: PointOnObject(g26,g4)
    c: Vertical(g26)
    c: PointOnObject(g27,g5)
    c: PointOnObject(g27,g2)
    c: Equal(g27,g26)
    c: Vertical(g27,g27)
    c: Vertical(g26,g27)
    c: PointOnObject(g28,g7)
    c: Horizontal(g28)
    c: PointOnObject(g29,g6)
    c: Coincident(g29,g8)
    c: Horizontal(g29)
    c: Equal(g16,g15)
    c: Equal(g14,g13)
    c: Angle(g16) = 1.309
    c: Angle(g13) = 1.74533
    c: Coincident(g30,g6)
    c: PointOnObject(g30,g3)
    c: Horizontal(g30)
    c: Coincident(g31,g6)
    c: PointOnObject(g31,g3)
    c: Horizontal(g31)
    c: Coincident(g32,g7)
    c: PointOnObject(g32,g1)
    c: Horizontal(g32)
    c: Coincident(g33,g7)
    c: PointOnObject(g33,g1)
    c: Horizontal(g33)
    c: Equal(g33,g31)
    c: PointOnObject(g34,g8)
    c: Horizontal(g8,g34)
    c: Angle(g15) = 1.309
    c: Angle(g14) = 1.74533
    c: DistanceX(g6,g7) = 17.526
    c: DistanceX(g6,g7) = 20.32
    c: DistanceX(g20,g29) = 5.8988
    c: DistanceX(g28,g21) = 5.8988
    c: Distance(g7) = 7.62
    c: Coincident(g35,g3)
    c: Coincident(g35,g10)
    c: Coincident(g36,g10)
    c: Coincident(g36,g0)
    c: Coincident(g37,g2)
    c: Coincident(g37,g17)
    c: Coincident(g38,g17)
    c: Coincident(g38,g3)
    c: Coincident(g39,g2)
    c: Coincident(g39,g12)
    c: Coincident(g40,g12)
    c: Coincident(g40,g1)
    c: Coincident(g41,g4)
    c: Coincident(g41,g5)
    c: Coincident(g42,g4)
    c: Coincident(g42,g5)
    c: DistanceY(g26,g26) = 0.278384
    c: DistanceX(g26,g0) = 15.24
    c: Coincident(g28,g9)
    c: DistanceX(g5,g5) = 15.24
    c: DistanceX(g4,g4) = 13.208
    c: DistanceY(g23,g33) = 2.794
    c: Radius(g11) = 0.828548
    c: Equal(g50,g49)
    c: Coincident(g53,g46)
    c: Coincident(g53,g43)
    c: Coincident(g54,g43)
    c: Coincident(g54,g44)
    c: Coincident(g55,g44)
    c: Coincident(g55,g45)
    c: Coincident(g56,g50)
    c: Coincident(g56,g48)
    c: Coincident(g57,g49)
    c: Coincident(g57,g48)
    c: Coincident(g58,g49)
    c: Coincident(g58,g47)
    c: Coincident(g59,g47)
    c: Coincident(g59,g50)
    c: Coincident(g60,g45)
    c: Coincident(g60,g46)
    c: Equal(g51,g52)
    c: Diameter(g51) = 2.2606
    c: DistanceX(g51,g52) = 24.9936
    c: DistanceX(g46,g44) = 30.8102
    c: Parallel(g48,g45)
    c: Parallel(g45,g47)
    c: Parallel(g47,g43)
    c: Parallel(g44,g46)
    c: Perpendicular(g44,g43)
    c: Coincident(g61,g43)
    c: Coincident(g61,g54)
    c: Vertical(g61)
    c: Coincident(g62,g54)
    c: Coincident(g62,g44)
    c: Horizontal(g62)
    c: Vertical(g54,g55)
    c: Vertical(g55,g45)
    c: Horizontal(g44,g55)
    c: Horizontal(g55,g60)
    c: Horizontal(g60,g46)
    c: Vertical(g45,g60)
    c: Vertical(g60,g53)
    c: Vertical(g53,g43)
    c: Horizontal(g46,g53)
    c: Horizontal(g53,g54)
    c: DistanceY(g45,g43) = 12.5984
    c: Coincident(g63,g51)
    c: PointOnObject(g63,g46)
    c: Horizontal(g63)
    c: Coincident(g64,g52)
    c: PointOnObject(g64,g44)
    c: Horizontal(g64)
    c: Equal(g64,g63)
    c: Coincident(g65,g51)
    c: PointOnObject(g65,g45)
    c: Vertical(g65)
    c: Coincident(g66,g52)
    c: PointOnObject(g66,g45)
    c: Vertical(g66)
    c: Coincident(g67,g51)
    c: PointOnObject(g67,g43)
    c: Vertical(g67)
    c: Coincident(g68,g52)
    c: PointOnObject(g68,g43)
    c: Vertical(g68)
    c: Equal(g68,g67)
    c: Equal(g68,g66)
    c: Horizontal(g49,g50)
    c: Horizontal(g50,g49)
    c: PointOnObject(g69,g43)
    c: PointOnObject(g69,g47)
    c: Vertical(g69)
    c: PointOnObject(g70,g48)
    c: PointOnObject(g70,g45)
    c: Equal(g70,g69)
    c: Vertical(g70,g70)
    c: Vertical(g69,g70)
    c: PointOnObject(g71,g50)
    c: Horizontal(g71)
    c: PointOnObject(g72,g49)
    c: Coincident(g72,g51)
    c: Horizontal(g72)
    c: Equal(g59,g58)
    c: Equal(g57,g56)
    c: Angle(g59) = 1.309
    c: Angle(g56) = 1.74533
    c: Coincident(g73,g49)
    c: PointOnObject(g73,g46)
    c: Horizontal(g73)
    c: Coincident(g74,g49)
    c: PointOnObject(g74,g46)
    c: Horizontal(g74)
    c: Coincident(g75,g50)
    c: PointOnObject(g75,g44)
    c: Horizontal(g75)
    c: Coincident(g76,g50)
    c: PointOnObject(g76,g44)
    c: Horizontal(g76)
    c: Equal(g76,g74)
    c: PointOnObject(g77,g51)
    c: Horizontal(g51,g77)
    c: Angle(g58) = 1.309
    c: Angle(g57) = 1.74533
    c: DistanceX(g49,g50) = 17.526
    c: DistanceX(g49,g50) = 20.32
    c: DistanceX(g63,g72) = 5.8988
    c: DistanceX(g71,g64) = 5.8988
    c: Distance(g50) = 7.62
    c: Coincident(g78,g46)
    c: Coincident(g78,g53)
    c: Coincident(g79,g53)
    c: Coincident(g79,g43)
    c: Coincident(g80,g45)
    c: Coincident(g80,g60)
    c: Coincident(g81,g60)
    c: Coincident(g81,g46)
    c: Coincident(g82,g45)
    c: Coincident(g82,g55)
    c: Coincident(g83,g55)
    c: Coincident(g83,g44)
    c: Coincident(g84,g47)
    c: Coincident(g84,g48)
    c: Coincident(g85,g47)
    c: Coincident(g85,g48)
    c: DistanceY(g69,g69) = 0.278384
    c: DistanceX(g69,g43) = 15.24
    c: Coincident(g71,g52)
    c: DistanceX(g48,g48) = 15.24
    c: DistanceX(g47,g47) = 13.208
    c: DistanceY(g66,g76) = 2.794
    c: Radius(g54) = 0.828548
    c: Equal(g93,g92)
    c: Coincident(g96,g89)
    c: Coincident(g96,g86)
    c: Coincident(g97,g86)
    c: Coincident(g97,g87)
    c: Coincident(g98,g87)
    c: Coincident(g98,g88)
    c: Coincident(g99,g93)
    c: Coincident(g99,g91)
    c: Coincident(g100,g92)
    c: Coincident(g100,g91)
    c: Coincident(g101,g92)
    c: Coincident(g101,g90)
    c: Coincident(g102,g90)
    c: Coincident(g102,g93)
    c: Coincident(g103,g88)
    c: Coincident(g103,g89)
    c: Equal(g94,g95)
    c: Diameter(g94) = 2.2606
    c: DistanceX(g94,g95) = 24.9936
    c: DistanceX(g89,g87) = 30.8102
    c: Parallel(g91,g88)
    c: Parallel(g88,g90)
    c: Parallel(g90,g86)
    c: Parallel(g87,g89)
    c: Perpendicular(g87,g86)
    c: Coincident(g104,g86)
    c: Coincident(g104,g97)
    c: Vertical(g104)
    c: Coincident(g105,g97)
    c: Coincident(g105,g87)
    c: Horizontal(g105)
    c: Vertical(g97,g98)
    c: Vertical(g98,g88)
    c: Horizontal(g87,g98)
    c: Horizontal(g98,g103)
    c: Horizontal(g103,g89)
    c: Vertical(g88,g103)
    c: Vertical(g103,g96)
    c: Vertical(g96,g86)
    c: Horizontal(g89,g96)
    c: Horizontal(g96,g97)
    c: DistanceY(g88,g86) = 12.5984
    c: Coincident(g106,g94)
    c: PointOnObject(g106,g89)
    c: Horizontal(g106)
    c: Coincident(g107,g95)
    c: PointOnObject(g107,g87)
    c: Horizontal(g107)
    c: Equal(g107,g106)
    c: Coincident(g108,g94)
    c: PointOnObject(g108,g88)
    c: Vertical(g108)
    c: Coincident(g109,g95)
    c: PointOnObject(g109,g88)
    c: Vertical(g109)
    c: Coincident(g110,g94)
    c: PointOnObject(g110,g86)
    c: Vertical(g110)
    c: Coincident(g111,g95)
    c: PointOnObject(g111,g86)
    c: Vertical(g111)
    c: Equal(g111,g110)
    c: Equal(g111,g109)
    c: Horizontal(g92,g93)
    c: Horizontal(g93,g92)
    c: PointOnObject(g112,g86)
    c: PointOnObject(g112,g90)
    c: Vertical(g112)
    c: PointOnObject(g113,g91)
    c: PointOnObject(g113,g88)
    c: Equal(g113,g112)
    c: Vertical(g113,g113)
    c: Vertical(g112,g113)
    c: PointOnObject(g114,g93)
    c: Horizontal(g114)
    c: PointOnObject(g115,g92)
    c: Coincident(g115,g94)
    c: Horizontal(g115)
    c: Equal(g102,g101)
    c: Equal(g100,g99)
    c: Angle(g102) = 1.309
    c: Angle(g99) = 1.74533
    c: Coincident(g116,g92)
    c: PointOnObject(g116,g89)
    c: Horizontal(g116)
    c: Coincident(g117,g92)
    c: PointOnObject(g117,g89)
    c: Horizontal(g117)
    c: Coincident(g118,g93)
    c: PointOnObject(g118,g87)
    c: Horizontal(g118)
    c: Coincident(g119,g93)
    c: PointOnObject(g119,g87)
    c: Horizontal(g119)
    c: Equal(g119,g117)
    c: PointOnObject(g120,g94)
    c: Horizontal(g94,g120)
    c: Angle(g101) = 1.309
    c: Angle(g100) = 1.74533
    c: DistanceX(g92,g93) = 17.526
    c: DistanceX(g92,g93) = 20.32
    c: DistanceX(g106,g115) = 5.8988
    c: DistanceX(g114,g107) = 5.8988
    c: Distance(g93) = 7.62
    c: Coincident(g121,g89)
    c: Coincident(g121,g96)
    c: Coincident(g122,g96)
    c: Coincident(g122,g86)
    c: Coincident(g123,g88)
    c: Coincident(g123,g103)
    c: Coincident(g124,g103)
    c: Coincident(g124,g89)
    c: Coincident(g125,g88)
    c: Coincident(g125,g98)
    c: Coincident(g126,g98)
    c: Coincident(g126,g87)
    c: Coincident(g127,g90)
    c: Coincident(g127,g91)
    c: Coincident(g128,g90)
    c: Coincident(g128,g91)
    c: DistanceY(g112,g112) = 0.278384
    c: DistanceX(g112,g86) = 15.24
    c: Coincident(g114,g95)
    c: DistanceX(g91,g91) = 15.24
    c: DistanceX(g90,g90) = 13.208
    c: DistanceY(g109,g119) = 2.794
    c: Radius(g97) = 0.828548
    c: Equal(g136,g135)
    c: Coincident(g139,g132)
    c: Coincident(g139,g129)
    c: Coincident(g140,g129)
    c: Coincident(g140,g130)
    c: Coincident(g141,g130)
    c: Coincident(g141,g131)
    c: Coincident(g142,g136)
    c: Coincident(g142,g134)
    c: Coincident(g143,g135)
    c: Coincident(g143,g134)
    c: Coincident(g144,g135)
    c: Coincident(g144,g133)
    c: Coincident(g145,g133)
    c: Coincident(g145,g136)
    c: Coincident(g146,g131)
    c: Coincident(g146,g132)
    c: Equal(g137,g138)
    c: Diameter(g137) = 2.2606
    c: DistanceX(g137,g138) = 24.9936
    c: DistanceX(g132,g130) = 30.8102
    c: Parallel(g134,g131)
    c: Parallel(g131,g133)
    c: Parallel(g133,g129)
    c: Parallel(g130,g132)
    c: Perpendicular(g130,g129)
    c: Coincident(g147,g129)
    c: Coincident(g147,g140)
    c: Vertical(g147)
    c: Coincident(g148,g140)
    c: Coincident(g148,g130)
    c: Horizontal(g148)
    c: Vertical(g140,g141)
    c: Vertical(g141,g131)
    c: Horizontal(g130,g141)
    c: Horizontal(g141,g146)
    c: Horizontal(g146,g132)
    c: Vertical(g131,g146)
    c: Vertical(g146,g139)
    c: Vertical(g139,g129)
    c: Horizontal(g132,g139)
    c: Horizontal(g139,g140)
    c: DistanceY(g131,g129) = 12.5984
    c: Coincident(g149,g137)
    c: PointOnObject(g149,g132)
    c: Horizontal(g149)
    c: Coincident(g150,g138)
    c: PointOnObject(g150,g130)
    c: Horizontal(g150)
    c: Equal(g150,g149)
    c: Coincident(g151,g137)
    c: PointOnObject(g151,g131)
    c: Vertical(g151)
    c: Coincident(g152,g138)
    c: PointOnObject(g152,g131)
    c: Vertical(g152)
    c: Coincident(g153,g137)
    c: PointOnObject(g153,g129)
    c: Vertical(g153)
    c: Coincident(g154,g138)
    c: PointOnObject(g154,g129)
    c: Vertical(g154)
    c: Equal(g154,g153)
    c: Equal(g154,g152)
    c: Horizontal(g135,g136)
    c: Horizontal(g136,g135)
    c: PointOnObject(g155,g129)
    c: PointOnObject(g155,g133)
    c: Vertical(g155)
    c: PointOnObject(g156,g134)
    c: PointOnObject(g156,g131)
    c: Equal(g156,g155)
    c: Vertical(g156,g156)
    c: Vertical(g155,g156)
    c: PointOnObject(g157,g136)
    c: Horizontal(g157)
    c: PointOnObject(g158,g135)
    c: Coincident(g158,g137)
    c: Horizontal(g158)
    c: Equal(g145,g144)
    c: Equal(g143,g142)
    c: Angle(g145) = 1.309
    c: Angle(g142) = 1.74533
    c: Coincident(g159,g135)
    c: PointOnObject(g159,g132)
    c: Horizontal(g159)
    c: Coincident(g160,g135)
    c: PointOnObject(g160,g132)
    c: Horizontal(g160)
    c: Coincident(g161,g136)
    c: PointOnObject(g161,g130)
    c: Horizontal(g161)
    c: Coincident(g162,g136)
    c: PointOnObject(g162,g130)
    c: Horizontal(g162)
    c: Equal(g162,g160)
    c: PointOnObject(g163,g137)
    c: Horizontal(g137,g163)
    c: Angle(g144) = 1.309
    c: Angle(g143) = 1.74533
    c: DistanceX(g135,g136) = 17.526
    c: DistanceX(g135,g136) = 20.32
    c: DistanceX(g149,g158) = 5.8988
    c: DistanceX(g157,g150) = 5.8988
    c: Distance(g136) = 7.62
    c: Coincident(g164,g132)
    c: Coincident(g164,g139)
    c: Coincident(g165,g139)
    c: Coincident(g165,g129)
    c: Coincident(g166,g131)
    c: Coincident(g166,g146)
    c: Coincident(g167,g146)
    c: Coincident(g167,g132)
    c: Coincident(g168,g131)
    c: Coincident(g168,g141)
    c: Coincident(g169,g141)
    c: Coincident(g169,g130)
    c: Coincident(g170,g133)
    c: Coincident(g170,g134)
    c: Coincident(g171,g133)
    c: Coincident(g171,g134)
    c: DistanceY(g155,g155) = 0.278384
    c: DistanceX(g155,g129) = 15.24
    c: Coincident(g157,g138)
    c: DistanceX(g134,g134) = 15.24
    c: DistanceX(g133,g133) = 13.208
    c: DistanceY(g152,g162) = 2.794
    c: Radius(g140) = 0.828548
    c: Horizontal(g95,g51)
    c: Horizontal(g8,g138)
    c: Vertical(g138,g95)
    c: Vertical(g8,g51)
    c: Coincident(g172,g69)
    c: PointOnObject(g172,g-3)
    c: Vertical(g172)
    c: Coincident(g173,g172)
    c: Coincident(g173,g27)
    c: Equal(g173,g172)
    c: Coincident(g174,g8)
    c: Coincident(g174,g138)
    c: Coincident(g175,g9)
    c: PointOnObject(g175,g-4)
    c: Horizontal(g175)
    c: Equal(g174,g175)
    c: DistanceX(g174,g174) = 25.4
    c: DistanceY(g173,g173) = 12.7
FEATURE [PartDesign::Pocket] Pocket  label="Feed_Throughs"
  BaseFeature = -> BaseFeature
  Direction = (0,0,-1)
  Length = 5
  Length2 = 5
  Profile = -> Sketch002
  ReferenceAxis = -> Sketch002 [N_Axis]
  Type = 1
FEATURE [PartDesign::Pocket] Pocket001  label="DSubs001"
  BaseFeature = -> Pocket
  Direction = (0,0,-1)
  Length = 5
  Length2 = 5
  Profile = -> Sketch011
  ReferenceAxis = -> Sketch011 [N_Axis]
  Type = 1
FEATURE [Sketcher::SketchObject] Sketch004  label="Circular_Connectors"
  ExternalGeometry = -> [DatumLine001,BaseFeature,Pocket001]
  FullyConstrained = true
  MapMode = 5
  Placement = pos=(0,0,71.9309) rot=(0,0,1;0rad)
  Support = -> [BaseFeature]
  expr: Constraints[101] = Constraints[49]
  expr: Constraints[60] = Constraints[8]
  expr: Constraints[70] = Constraints[18]
  expr: Constraints[88] = Constraints[36]
  expr: Constraints[99] = Constraints[47]
  sketch-geometry (37):
    g0: LineSegment StartX=182.608 StartY=-89.7456 StartZ=0 EndX=203.233 EndY=-89.7456 EndZ=0
    g1: LineSegment StartX=203.233 StartY=-89.7456 StartZ=0 EndX=203.233 EndY=-110.37 EndZ=0
    g2: LineSegment StartX=203.233 StartY=-110.37 StartZ=0 EndX=182.608 EndY=-110.37 EndZ=0
    g3: LineSegment StartX=182.608 StartY=-110.37 StartZ=0 EndX=182.608 EndY=-89.7456 EndZ=0
    g4: Circle CenterX=192.92 CenterY=-100.058 CenterZ=0 NormalX=0 NormalY=0 NormalZ=1 AngleXU=0 Radius=6.35
    g5: Circle CenterX=200.464 CenterY=-92.5142 CenterZ=0 NormalX=0 NormalY=0 NormalZ=1 AngleXU=0 Radius=1.1303
    g6: Circle CenterX=200.464 CenterY=-107.602 CenterZ=0 NormalX=0 NormalY=0 NormalZ=1 AngleXU=0 Radius=1.1303
    g7: Circle CenterX=185.377 CenterY=-92.5142 CenterZ=0 NormalX=0 NormalY=0 NormalZ=1 AngleXU=0 Radius=1.1303
    g8: Circle CenterX=185.377 CenterY=-107.602 CenterZ=0 NormalX=0 NormalY=0 NormalZ=1 AngleXU=0 Radius=1.1303
    g9: LineSegment StartX=192.92 StartY=-89.7456 StartZ=0 EndX=192.92 EndY=-93.708 EndZ=0
    g10: LineSegment StartX=192.92 StartY=-106.408 StartZ=0 EndX=192.92 EndY=-110.37 EndZ=0
    g11: LineSegment StartX=186.57 StartY=-100.058 StartZ=0 EndX=182.608 EndY=-100.058 EndZ=0
    g12: LineSegment StartX=199.27 StartY=-100.058 StartZ=0 EndX=203.233 EndY=-100.058 EndZ=0
    g13: LineSegment StartX=200.464 StartY=-92.5142 StartZ=0 EndX=200.464 EndY=-89.7456 EndZ=0
    g14: LineSegment StartX=200.464 StartY=-92.5142 StartZ=0 EndX=203.233 EndY=-92.5142 EndZ=0
    g15: LineSegment StartX=185.377 StartY=-107.602 StartZ=0 EndX=182.608 EndY=-107.602 EndZ=0
    g16: LineSegment StartX=185.377 StartY=-107.602 StartZ=0 EndX=185.377 EndY=-110.37 EndZ=0
    g17: LineSegment StartX=182.608 StartY=-43.658 StartZ=0 EndX=203.233 EndY=-43.658 EndZ=0
    g18: LineSegment StartX=203.233 StartY=-43.658 StartZ=0 EndX=203.233 EndY=-64.2828 EndZ=0
    g19: LineSegment StartX=203.233 StartY=-64.2828 StartZ=0 EndX=182.608 EndY=-64.2828 EndZ=0
    g20: LineSegment StartX=182.608 StartY=-64.2828 StartZ=0 EndX=182.608 EndY=-43.658 EndZ=0
    g21: Circle CenterX=192.92 CenterY=-53.9704 CenterZ=0 NormalX=0 NormalY=0 NormalZ=1 AngleXU=0 Radius=6.35
    g22: Circle CenterX=200.464 CenterY=-46.4266 CenterZ=0 NormalX=0 NormalY=0 NormalZ=1 AngleXU=0 Radius=1.1303
    g23: Circle CenterX=200.464 CenterY=-61.5142 CenterZ=0 NormalX=0 NormalY=0 NormalZ=1 AngleXU=0 Radius=1.1303
    g24: Circle CenterX=185.377 CenterY=-46.4266 CenterZ=0 NormalX=0 NormalY=0 NormalZ=1 AngleXU=0 Radius=1.1303
    g25: Circle CenterX=185.377 CenterY=-61.5142 CenterZ=0 NormalX=0 NormalY=0 NormalZ=1 AngleXU=0 Radius=1.1303
    g26: LineSegment StartX=192.92 StartY=-43.658 StartZ=0 EndX=192.92 EndY=-47.6204 EndZ=0
    g27: LineSegment StartX=192.92 StartY=-60.3204 StartZ=0 EndX=192.92 EndY=-64.2828 EndZ=0
    g28: LineSegment StartX=186.57 StartY=-53.9704 StartZ=0 EndX=182.608 EndY=-53.9704 EndZ=0
    g29: LineSegment StartX=199.27 StartY=-53.9704 StartZ=0 EndX=203.233 EndY=-53.9704 EndZ=0
    g30: LineSegment StartX=200.464 StartY=-46.4266 StartZ=0 EndX=200.464 EndY=-43.658 EndZ=0
    g31: LineSegment StartX=200.464 StartY=-46.4266 StartZ=0 EndX=203.233 EndY=-46.4266 EndZ=0
    g32: LineSegment StartX=185.377 StartY=-61.5142 StartZ=0 EndX=182.608 EndY=-61.5142 EndZ=0
    g33: LineSegment StartX=185.377 StartY=-61.5142 StartZ=0 EndX=185.377 EndY=-64.2828 EndZ=0
    g34: LineSegment StartX=192.92 StartY=-64.2828 StartZ=0 EndX=192.92 EndY=-77.0142 EndZ=0
    g35: LineSegment StartX=192.92 StartY=-77.0142 StartZ=0 EndX=192.92 EndY=-89.7456 EndZ=0
    g36: LineSegment StartX=200.464 StartY=-61.5142 StartZ=0 EndX=225.864 EndY=-61.5142 EndZ=0
  constraints (119):
    c: Coincident(g0,g1)
    c: Coincident(g1,g2)
    c: Coincident(g2,g3)
    c: Coincident(g3,g0)
    c: Horizontal(g0)
    c: Horizontal(g2)
    c: Vertical(g1)
    c: Vertical(g3)
    c: DistanceX(g0,g0) = 20.6248
    c: Equal(g2,g1)
    c: PointOnObject(g9,g0)
    c: PointOnObject(g10,g2)
    c: Equal(g6,g8)
    c: Equal(g8,g7)
    c: Equal(g7,g5)
    c: Horizontal(g6,g8)
    c: Vertical(g7,g8)
    c: Horizontal(g7,g5)
    c: DistanceX(g8,g6) = 15.0876
    c: PointOnObject(g9,g4)
    c: Vertical(g9,g9)
    c: Vertical(g6,g5)
    c: PointOnObject(g10,g4)
    c: Vertical(g10,g10)
    c: PointOnObject(g11,g4)
    c: PointOnObject(g11,g3)
    c: Horizontal(g11)
    c: PointOnObject(g12,g4)
    c: PointOnObject(g12,g1)
    c: Horizontal(g12)
    c: Horizontal(g4,g12)
    c: Horizontal(g11,g4)
    c: Vertical(g4,g10)
    c: Coincident(g13,g5)
    c: PointOnObject(g13,g0)
    c: Vertical(g13)
    c: DistanceY(g6,g5) = 15.0876
    c: Coincident(g14,g5)
    c: PointOnObject(g14,g1)
    c: Horizontal(g14)
    c: Equal(g14,g13)
    c: Coincident(g15,g8)
    c: PointOnObject(g15,g3)
    c: Horizontal(g15)
    c: PointOnObject(g16,g15)
    c: PointOnObject(g16,g2)
    c: Vertical(g16)
    c: DistanceX(g15,g8) = 2.7686
    c: Vertical(g16,g8)
    c: Diameter(g5) = 2.2606
    c: Equal(g9,g12)
    c: Equal(g12,g10)
    c: Coincident(g17,g18)
    c: Coincident(g18,g19)
    c: Coincident(g19,g20)
    c: Coincident(g20,g17)
    c: Horizontal(g17)
    c: Horizontal(g19)
    c: Vertical(g18)
    c: Vertical(g20)
    c: DistanceX(g17,g17) = 20.6248
    c: Equal(g19,g18)
    c: PointOnObject(g26,g17)
    c: PointOnObject(g27,g19)
    c: Equal(g23,g25)
    c: Equal(g25,g24)
    c: Equal(g24,g22)
    c: Horizontal(g23,g25)
    c: Vertical(g24,g25)
    c: Horizontal(g24,g22)
    c: DistanceX(g25,g23) = 15.0876
    c: PointOnObject(g26,g21)
    c: Vertical(g26,g26)
    c: Vertical(g23,g22)
    c: PointOnObject(g27,g21)
    c: Vertical(g27,g27)
    c: PointOnObject(g28,g21)
    c: PointOnObject(g28,g20)
    c: Horizontal(g28)
    c: PointOnObject(g29,g21)
    c: PointOnObject(g29,g18)
    c: Horizontal(g29)
    c: Horizontal(g21,g29)
    c: Horizontal(g28,g21)
    c: Vertical(g21,g27)
    c: Coincident(g30,g22)
    c: PointOnObject(g30,g17)
    c: Vertical(g30)
    c: DistanceY(g23,g22) = 15.0876
    c: Coincident(g31,g22)
    c: PointOnObject(g31,g18)
    c: Horizontal(g31)
    c: Equal(g31,g30)
    c: Coincident(g32,g25)
    c: PointOnObject(g32,g20)
    c: Horizontal(g32)
    c: PointOnObject(g33,g32)
    c: PointOnObject(g33,g19)
    c: Vertical(g33)
    c: DistanceX(g32,g25) = 2.7686
    c: Vertical(g33,g25)
    c: Diameter(g22) = 2.2606
    c: Equal(g26,g29)
    c: Equal(g29,g27)
    c: Equal(g27,g28)
    c: Vertical(g18,g0)
    c: Coincident(g34,g27)
    c: PointOnObject(g34,g-3)
    c: Vertical(g34)
    c: Coincident(g35,g34)
    c: Coincident(g35,g9)
    c: Vertical(g35)
    c: Equal(g34,g35)
    c: Horizontal(g23,g-6)
    c: Coincident(g36,g23)
    c: Coincident(g36,g-6)
    c: DistanceX(g36,g36) = 25.4
    c: Diameter(g21) = 12.7
    c: Equal(g4,g21)
FEATURE [PartDesign::Pocket] Pocket002  label="Circular_Connectors001"
  BaseFeature = -> Pocket001
  Direction = (0,0,-1)
  Length = 5
  Length2 = 5
  Profile = -> Sketch004
  ReferenceAxis = -> Sketch004 [N_Axis]
  Type = 1
FEATURE [TechDraw::DrawSVGTemplate] Template
  EditableTexts = AUTHOR_NAME=Dennis H. Calderon; DN=DN; DRAWING_TITLE=DCT_HSK_Box_Front_Panel; FC-DATE=03/15/2023; FC-REV=REV A; FC-SH=1/1; FC-SI=A4; FreeCAD_DRAWING=HELIX; PN=PN; SI-1=The Ohio State University
  Height = 210
  Orientation = 1
  Width = 297
FEATURE [TechDraw::DrawViewPart] View001  label="DSUB_Connector"
  CoarseView = false
  Direction = (0,0,1)
  Focus = 100
  HardHidden = false
  IsoCount = 0
  IsoHidden = false
  IsoVisible = false
  LockPosition = false
  Perspective = false
  Rotation = 0
  ScaleType = 0
  SeamHidden = false
  SeamVisible = true
  SmoothHidden = false
  SmoothVisible = true
  Source = -> [Sketch010]
  X = 190.561
  XDirection = (1,0,0)
  Y = 161.562
FEATURE [Sketcher::SketchObject] Sketch  label="Circular_Connectors002"
  ExternalGeometry = -> [DatumLine001,BaseFeature,Pocket001]
  FullyConstrained = true
  MapMode = 5
  Support = -> [XY_Plane]
  expr: Constraints[18] = Sketch004.Constraints[70]
  expr: Constraints[36] = Sketch004.Constraints[88]
  expr: Constraints[47] = Sketch004.Constraints[99]
  expr: Constraints[49] = Sketch004.Constraints[101]
  expr: Constraints[62] = Sketch004.Constraints[116]
  expr: Constraints[63] = Sketch004.Constraints[117]
  expr: Constraints[8] = Sketch004.Constraints[60]
  sketch-geometry (20):
    g0: LineSegment StartX=182.608 StartY=-43.658 StartZ=0 EndX=203.233 EndY=-43.658 EndZ=0
    g1: LineSegment StartX=203.233 StartY=-43.658 StartZ=0 EndX=203.233 EndY=-64.2828 EndZ=0
    g2: LineSegment StartX=203.233 StartY=-64.2828 StartZ=0 EndX=182.608 EndY=-64.2828 EndZ=0
    g3: LineSegment StartX=182.608 StartY=-64.2828 StartZ=0 EndX=182.608 EndY=-43.658 EndZ=0
    g4: Circle CenterX=192.92 CenterY=-53.9704 CenterZ=0 NormalX=0 NormalY=0 NormalZ=1 AngleXU=0 Radius=6.35
    g5: Circle CenterX=200.464 CenterY=-46.4266 CenterZ=0 NormalX=0 NormalY=0 NormalZ=1 AngleXU=0 Radius=1.1303
    g6: Circle CenterX=200.464 CenterY=-61.5142 CenterZ=0 NormalX=0 NormalY=0 NormalZ=1 AngleXU=0 Radius=1.1303
    g7: Circle CenterX=185.377 CenterY=-46.4266 CenterZ=0 NormalX=0 NormalY=0 NormalZ=1 AngleXU=0 Radius=1.1303
    g8: Circle CenterX=185.377 CenterY=-61.5142 CenterZ=0 NormalX=0 NormalY=0 NormalZ=1 AngleXU=0 Radius=1.1303
    g9: LineSegment StartX=192.92 StartY=-43.658 StartZ=0 EndX=192.92 EndY=-47.6204 EndZ=0
    g10: LineSegment StartX=192.92 StartY=-60.3204 StartZ=0 EndX=192.92 EndY=-64.2828 EndZ=0
    g11: LineSegment StartX=186.57 StartY=-53.9704 StartZ=0 EndX=182.608 EndY=-53.9704 EndZ=0
    g12: LineSegment StartX=199.27 StartY=-53.9704 StartZ=0 EndX=203.233 EndY=-53.9704 EndZ=0
    g13: LineSegment StartX=200.464 StartY=-46.4266 StartZ=0 EndX=200.464 EndY=-43.658 EndZ=0
    g14: LineSegment StartX=200.464 StartY=-46.4266 StartZ=0 EndX=203.233 EndY=-46.4266 EndZ=0
    g15: LineSegment StartX=185.377 StartY=-61.5142 StartZ=0 EndX=182.608 EndY=-61.5142 EndZ=0
    g16: LineSegment StartX=185.377 StartY=-61.5142 StartZ=0 EndX=185.377 EndY=-64.2828 EndZ=0
    g17: LineSegment StartX=192.92 StartY=-64.2828 StartZ=0 EndX=192.92 EndY=-77.0142 EndZ=0
    g18: LineSegment StartX=192.92 StartY=-77.0142 StartZ=0 EndX=192.92 EndY=-89.7456 EndZ=0
    g19: LineSegment StartX=200.464 StartY=-61.5142 StartZ=0 EndX=225.864 EndY=-61.5142 EndZ=0
  constraints (64):
    c: Coincident(g0,g1)
    c: Coincident(g1,g2)
    c: Coincident(g2,g3)
    c: Coincident(g3,g0)
    c: Horizontal(g0)
    c: Horizontal(g2)
    c: Vertical(g1)
    c: Vertical(g3)
    c: DistanceX(g0,g0) = 20.6248
    c: Equal(g2,g1)
    c: PointOnObject(g9,g0)
    c: PointOnObject(g10,g2)
    c: Equal(g6,g8)
    c: Equal(g8,g7)
    c: Equal(g7,g5)
    c: Horizontal(g6,g8)
    c: Vertical(g7,g8)
    c: Horizontal(g7,g5)
    c: DistanceX(g8,g6) = 15.0876
    c: PointOnObject(g9,g4)
    c: Vertical(g9,g9)
    c: Vertical(g6,g5)
    c: PointOnObject(g10,g4)
    c: Vertical(g10,g10)
    c: PointOnObject(g11,g4)
    c: PointOnObject(g11,g3)
    c: Horizontal(g11)
    c: PointOnObject(g12,g4)
    c: PointOnObject(g12,g1)
    c: Horizontal(g12)
    c: Horizontal(g4,g12)
    c: Horizontal(g11,g4)
    c: Vertical(g4,g10)
    c: Coincident(g13,g5)
    c: PointOnObject(g13,g0)
    c: Vertical(g13)
    c: DistanceY(g6,g5) = 15.0876
    c: Coincident(g14,g5)
    c: PointOnObject(g14,g1)
    c: Horizontal(g14)
    c: Equal(g14,g13)
    c: Coincident(g15,g8)
    c: PointOnObject(g15,g3)
    c: Horizontal(g15)
    c: PointOnObject(g16,g15)
    c: PointOnObject(g16,g2)
    c: Vertical(g16)
    c: DistanceX(g15,g8) = 2.7686
    c: Vertical(g16,g8)
    c: Diameter(g5) = 2.2606
    c: Equal(g9,g12)
    c: Equal(g12,g10)
    c: Equal(g10,g11)
    c: Coincident(g17,g10)
    c: PointOnObject(g17,g-3)
    c: Vertical(g17)
    c: Coincident(g18,g17)
    c: Vertical(g18)
    c: Equal(g17,g18)
    c: Horizontal(g6,g-6)
    c: Coincident(g19,g6)
    c: Coincident(g19,g-6)
    c: DistanceX(g19,g19) = 25.4
    c: Diameter(g4) = 12.7
FEATURE [TechDraw::DrawViewPart] View002  label="Circuilar_connector"
  CoarseView = false
  Direction = (0,0,1)
  Focus = 100
  HardHidden = false
  IsoCount = 0
  IsoHidden = false
  IsoVisible = false
  LockPosition = false
  Perspective = false
  Rotation = 0
  ScaleType = 0
  SeamHidden = false
  SeamVisible = true
  SmoothHidden = false
  SmoothVisible = true
  Source = -> [Sketch]
  X = 263.007
  XDirection = (1,0,0)
  Y = 159.542
FEATURE [Sketcher::SketchObject] Sketch012  label="Feed_through"
  ExternalGeometry = -> [BaseFeature]
  FullyConstrained = false
  MapMode = 2
  Support = -> [BaseFeature]
  expr: Constraints[13] = Sketch002.Constraints[258]
  expr: Constraints[22] = Sketch002.Constraints[267]
  expr: Constraints[23] = Sketch002.Constraints[268]
  expr: Constraints[5] = Sketch002.Constraints[250]
  expr: Constraints[60] = Sketch002.Constraints[305]
  expr: Constraints[64] = Sketch002.Constraints[309]
  expr: Constraints[65] = Sketch002.Constraints[310]
  sketch-geometry (32):
    g0: LineSegment StartX=-32.0861 StartY=-110.421 StartZ=0 EndX=-32.0861 EndY=-90.279 EndZ=0
    g1: ArcOfCircle CenterX=-99.5518 CenterY=-100.35 CenterZ=0 NormalX=0 NormalY=0 NormalZ=1 AngleXU=0 Radius=9.2456 StartAngle=1.5708 EndAngle=4.71239
    g2: ArcOfCircle CenterX=-52.003 CenterY=-100.35 CenterZ=0 NormalX=0 NormalY=0 NormalZ=1 AngleXU=0 Radius=9.2456 StartAngle=4.71239 EndAngle=7.85398
    g3: LineSegment StartX=-99.5518 StartY=-109.596 StartZ=0 EndX=-52.003 EndY=-109.596 EndZ=0
    g4: LineSegment StartX=-52.003 StartY=-91.1045 StartZ=0 EndX=-99.5518 EndY=-91.1045 EndZ=0
    g5: LineSegment StartX=-42.7574 StartY=-110.421 StartZ=0 EndX=-42.7574 EndY=-90.279 EndZ=0
    g6: LineSegment StartX=-108.797 StartY=-90.279 StartZ=0 EndX=-108.797 EndY=-110.421 EndZ=0
    g7: LineSegment StartX=-113.369 StartY=-90.279 StartZ=0 EndX=-38.1854 EndY=-90.279 EndZ=0
    g8: LineSegment StartX=-38.1854 StartY=-90.279 StartZ=0 EndX=-38.1854 EndY=-110.421 EndZ=0
    g9: LineSegment StartX=-38.1854 StartY=-110.421 StartZ=0 EndX=-113.369 EndY=-110.421 EndZ=0
    g10: LineSegment StartX=-113.369 StartY=-110.421 StartZ=0 EndX=-113.369 EndY=-90.279 EndZ=0
    g11: LineSegment StartX=-108.797 StartY=-100.35 StartZ=0 EndX=-113.369 EndY=-100.35 EndZ=0
    g12: LineSegment StartX=-42.7574 StartY=-100.35 StartZ=0 EndX=-38.1854 EndY=-100.35 EndZ=0
    g13: LineSegment StartX=-75.7774 StartY=-91.1045 StartZ=0 EndX=-75.7774 EndY=-90.279 EndZ=0
    g14: LineSegment StartX=-75.7774 StartY=-110.421 StartZ=0 EndX=-75.7774 EndY=-109.596 EndZ=0
    g15: LineSegment StartX=-108.797 StartY=-100.35 StartZ=0 EndX=-42.7574 EndY=-100.35 EndZ=0
    g16: LineSegment StartX=-75.7774 StartY=-91.1045 StartZ=0 EndX=-75.7774 EndY=-109.596 EndZ=0
    g17: GeomPoint X=-75.7774 Y=-100.35 Z=0
    g18: LineSegment StartX=-42.7574 StartY=-90.279 StartZ=0 EndX=-75.7774 EndY=-90.279 EndZ=0
    g19: LineSegment StartX=-75.7774 StartY=-90.279 StartZ=0 EndX=-108.797 EndY=-90.279 EndZ=0
    g20: LineSegment StartX=-108.797 StartY=-110.421 StartZ=0 EndX=-113.369 EndY=-110.421 EndZ=0
    g21: LineSegment StartX=-38.1854 StartY=-110.421 StartZ=0 EndX=-42.7574 EndY=-110.421 EndZ=0
    g22: Circle CenterX=-40.8524 CenterY=-92.5142 CenterZ=0 NormalX=0 NormalY=0 NormalZ=1 AngleXU=0 Radius=1.1303
    g23: Circle CenterX=-40.8524 CenterY=-107.754 CenterZ=0 NormalX=0 NormalY=0 NormalZ=1 AngleXU=0 Radius=1.1303
    g24: Circle CenterX=-110.702 CenterY=-92.5142 CenterZ=0 NormalX=0 NormalY=0 NormalZ=1 AngleXU=0 Radius=1.1303
    g25: Circle CenterX=-110.702 CenterY=-107.754 CenterZ=0 NormalX=0 NormalY=0 NormalZ=1 AngleXU=0 Radius=1.1303
    g26: LineSegment StartX=-40.8524 StartY=-107.754 StartZ=0 EndX=-38.1854 EndY=-107.754 EndZ=0
    g27: LineSegment StartX=-40.8524 StartY=-107.754 StartZ=0 EndX=-40.8524 EndY=-110.421 EndZ=0
    g28: LineSegment StartX=-110.702 StartY=-107.754 StartZ=0 EndX=-110.702 EndY=-110.421 EndZ=0
    g29: LineSegment StartX=-110.702 StartY=-107.754 StartZ=0 EndX=-113.369 EndY=-107.754 EndZ=0
    g30: LineSegment StartX=-75.7774 StartY=-110.421 StartZ=0 EndX=-75.7774 EndY=-142.014 EndZ=0
    g31: LineSegment StartX=-122.136 StartY=-92.5142 StartZ=0 EndX=-110.702 EndY=-92.5142 EndZ=0
  constraints (89):
    c: Vertical(g0)
    c: Tangent(g1,g3) = -1.5708
    c: Tangent(g3,g2) = -1.5708
    c: Tangent(g2,g4) = -1.5708
    c: Tangent(g4,g1) = -1.5708
    c: DistanceY(g2,g2) = 18.4912
    c: Horizontal(g2,g1)
    c: Horizontal(g1,g2)
    c: Vertical(g5)
    c: Vertical(g6)
    c: Tangent(g6,g1)
    c: Tangent(g5,g2)
    c: Horizontal(g6,g5)
    c: DistanceX(g6,g5) = 66.04
    c: Coincident(g7,g8)
    c: Coincident(g8,g9)
    c: Coincident(g9,g10)
    c: Coincident(g10,g7)
    c: Horizontal(g7)
    c: Horizontal(g9)
    c: Vertical(g8)
    c: Vertical(g10)
    c: DistanceX(g7,g7) = 75.184
    c: DistanceY(g8,g8) = 20.1422
    c: PointOnObject(g11,g6)
    c: PointOnObject(g11,g10)
    c: Horizontal(g11)
    c: PointOnObject(g12,g5)
    c: PointOnObject(g12,g8)
    c: Horizontal(g12)
    c: Equal(g12,g11)
    c: PointOnObject(g13,g4)
    c: PointOnObject(g13,g7)
    c: Vertical(g13)
    c: PointOnObject(g14,g9)
    c: PointOnObject(g14,g3)
    c: Vertical(g14)
    c: Equal(g14,g13)
    c: Equal(g6,g10)
    c: Horizontal(g6,g7)
    c: Horizontal(g1,g11)
    c: Horizontal(g2,g12)
    c: Coincident(g15,g11)
    c: Coincident(g15,g12)
    c: Coincident(g16,g13)
    c: Coincident(g16,g14)
    c: Vertical(g16)
    c: PointOnObject(g17,g15)
    c: Vertical(g17,g13)
    c: Horizontal(g5,g7)
    c: Coincident(g18,g5)
    c: Coincident(g18,g13)
    c: Coincident(g19,g13)
    c: Coincident(g19,g6)
    c: Equal(g18,g19)
    c: Coincident(g20,g6)
    c: Coincident(g20,g9)
    c: Coincident(g21,g8)
    c: Coincident(g21,g5)
    c: Vertical(g23,g22)
    c: Diameter(g24) = 2.2606
    c: Vertical(g24,g25)
    c: Horizontal(g25,g23)
    c: Horizontal(g24,g22)
    c: DistanceY(g23,g22) = 15.24
    c: DistanceX(g25,g23) = 69.85
    c: Coincident(g26,g23)
    c: PointOnObject(g26,g8)
    c: Horizontal(g26)
    c: Coincident(g27,g23)
    c: PointOnObject(g27,g9)
    c: Vertical(g27)
    c: Equal(g26,g27)
    c: Coincident(g28,g25)
    c: PointOnObject(g28,g9)
    c: Vertical(g28)
    c: Coincident(g29,g25)
    c: PointOnObject(g29,g10)
    c: Horizontal(g29)
    c: Equal(g29,g28)
    c: Equal(g25,g24)
    c: Equal(g24,g22)
    c: Equal(g22,g23)
    c: Coincident(g30,g14)
    c: PointOnObject(g30,g-4)
    c: Vertical(g30)
    c: Coincident(g31,g-5)
    c: Coincident(g31,g24)
    c: Horizontal(g31)
FEATURE [TechDraw::DrawViewDimension] Dimension
  AngleOverride = false
  Arbitrary = false
  ArbitraryTolerances = false
  EqualTolerance = true
  ExtensionAngle = 0
  FormatSpec = ⌀%.3w
  FormatSpecOverTolerance = %+.2w
  FormatSpecUnderTolerance = %+.2w
  Inverted = false
  LineAngle = 0
  LockPosition = false
  MeasureType = 1
  OverTolerance = 0
  References2D = -> [View002]
  Rotation = 0
  ScaleType = 0
  TheoreticalExact = false
  Type = 5
  UnderTolerance = 0
  X = -20.2392
  Y = 6.72207
FEATURE [TechDraw::DrawViewDimension] Dimension007
  AngleOverride = false
  Arbitrary = false
  ArbitraryTolerances = false
  EqualTolerance = true
  ExtensionAngle = 0
  FormatSpec = %.2w
  FormatSpecOverTolerance = %+.2w
  FormatSpecUnderTolerance = %+.2w
  Inverted = false
  LineAngle = 0
  LockPosition = false
  MeasureType = 1
  OverTolerance = 0
  References2D = -> [View002]
  Rotation = 0
  ScaleType = 0
  TheoreticalExact = false
  Type = 2
  UnderTolerance = 0
  X = 18.0715
  Y = 3.18035
FEATURE [TechDraw::DrawViewDimension] Dimension010
  AngleOverride = false
  Arbitrary = false
  ArbitraryTolerances = false
  EqualTolerance = true
  ExtensionAngle = 0
  FormatSpec = %.2w
  FormatSpecOverTolerance = %+.2w
  FormatSpecUnderTolerance = %+.2w
  Inverted = false
  LineAngle = 0
  LockPosition = false
  MeasureType = 1
  OverTolerance = 0
  References2D = -> [View001]
  Rotation = 0
  ScaleType = 2
  TheoreticalExact = false
  Type = 1
  UnderTolerance = 0
  X = 0.863656
  Y = -16.5772
FEATURE [TechDraw::DrawViewDimension] Dimension011
  AngleOverride = false
  Arbitrary = false
  ArbitraryTolerances = false
  EqualTolerance = true
  ExtensionAngle = 0
  FormatSpec = ⌀%.3w
  FormatSpecOverTolerance = %+.2w
  FormatSpecUnderTolerance = %+.2w
  Inverted = false
  LineAngle = 0
  LockPosition = false
  MeasureType = 1
  OverTolerance = 0
  References2D = -> [View001]
  Rotation = 0
  ScaleType = 2
  TheoreticalExact = false
  Type = 5
  UnderTolerance = 0
  X = -24.4778
  Y = 5.46048
FEATURE [TechDraw::DrawViewPart] View003  label="Feed_through001"
  CoarseView = false
  Direction = (0,0,1)
  Focus = 100
  HardHidden = false
  IsoCount = 0
  IsoHidden = false
  IsoVisible = false
  LockPosition = false
  Perspective = false
  Rotation = 0
  ScaleType = 0
  SeamHidden = false
  SeamVisible = true
  SmoothHidden = false
  SmoothVisible = true
  Source = -> [Sketch012]
  X = 69.3634
  XDirection = (1,0,0)
  Y = 162.225
FEATURE [TechDraw::DrawViewDimension] Dimension018
  AngleOverride = false
  Arbitrary = false
  ArbitraryTolerances = false
  EqualTolerance = true
  ExtensionAngle = 0
  FormatSpec = %.2w
  FormatSpecOverTolerance = %+.2w
  FormatSpecUnderTolerance = %+.2w
  Inverted = false
  LineAngle = 0
  LockPosition = false
  MeasureType = 1
  OverTolerance = 0
  References2D = -> [View001]
  Rotation = 0
  ScaleType = 2
  TheoreticalExact = false
  Type = 1
  UnderTolerance = 0
  X = -0.37475
  Y = -9.67524
FEATURE [TechDraw::DrawViewDimension] Dimension019
  AngleOverride = false
  Arbitrary = false
  ArbitraryTolerances = false
  EqualTolerance = true
  ExtensionAngle = 0
  FormatSpec = %.2w
  FormatSpecOverTolerance = %+.2w
  FormatSpecUnderTolerance = %+.2w
  Inverted = false
  LineAngle = 0
  LockPosition = false
  MeasureType = 1
  OverTolerance = 0
  References2D = -> [View001]
  Rotation = 0
  ScaleType = 2
  TheoreticalExact = false
  Type = 1
  UnderTolerance = 0
  X = 0.756372
  Y = 19.7936
FEATURE [TechDraw::DrawViewDimension] Dimension022
  AngleOverride = false
  Arbitrary = false
  ArbitraryTolerances = false
  EqualTolerance = true
  ExtensionAngle = 0
  FormatSpec = %.2w
  FormatSpecOverTolerance = %+.2w
  FormatSpecUnderTolerance = %+.2w
  Inverted = false
  LineAngle = 0
  LockPosition = false
  MeasureType = 1
  OverTolerance = 0
  References2D = -> [View001]
  Rotation = 0
  ScaleType = 2
  TheoreticalExact = false
  Type = 0
  UnderTolerance = 0
  X = 19.293
  Y = 2.03416
FEATURE [TechDraw::DrawViewDimension] Dimension023
  AngleOverride = false
  Arbitrary = false
  ArbitraryTolerances = false
  EqualTolerance = true
  ExtensionAngle = 0
  FormatSpec = ⌀%.2w
  FormatSpecOverTolerance = %+.2w
  FormatSpecUnderTolerance = %+.2w
  Inverted = false
  LineAngle = 0
  LockPosition = false
  MeasureType = 1
  OverTolerance = 0
  References2D = -> [View002]
  Rotation = 0
  ScaleType = 2
  TheoreticalExact = false
  Type = 5
  UnderTolerance = 0
  X = -22.0934
  Y = -6.3731
FEATURE [TechDraw::DrawViewDimension] Dimension026
  AngleOverride = false
  Arbitrary = false
  ArbitraryTolerances = false
  EqualTolerance = true
  ExtensionAngle = 0
  FormatSpec = %.2w
  FormatSpecOverTolerance = %+.2w
  FormatSpecUnderTolerance = %+.2w
  Inverted = false
  LineAngle = 0
  LockPosition = false
  MeasureType = 1
  OverTolerance = 0
  References2D = -> [View001]
  Rotation = 0
  ScaleType = 2
  TheoreticalExact = false
  Type = 1
  UnderTolerance = 0
  X = 21.0203
  Y = 15.6151
FEATURE [TechDraw::DrawViewDimension] Dimension027
  AngleOverride = false
  Arbitrary = false
  ArbitraryTolerances = false
  EqualTolerance = true
  ExtensionAngle = 0
  FormatSpec = %.2w
  FormatSpecOverTolerance = %+.2w
  FormatSpecUnderTolerance = %+.2w
  Inverted = false
  LineAngle = 0
  LockPosition = false
  MeasureType = 1
  OverTolerance = 0
  References2D = -> [View001]
  Rotation = 0
  ScaleType = 2
  TheoreticalExact = false
  Type = 2
  UnderTolerance = 0
  X = 32.5896
  Y = 12.872
FEATURE [TechDraw::DrawViewDimension] Dimension034
  AngleOverride = false
  Arbitrary = false
  ArbitraryTolerances = false
  EqualTolerance = true
  ExtensionAngle = 0
  FormatSpec = %.4w
  FormatSpecOverTolerance = %+.2w
  FormatSpecUnderTolerance = %+.2w
  Inverted = false
  LineAngle = 0
  LockPosition = false
  MeasureType = 1
  OverTolerance = 0
  References2D = -> [View003]
  Rotation = 0
  ScaleType = 2
  TheoreticalExact = false
  Type = 2
  UnderTolerance = 0
  X = 41.3262
  Y = 2.09633
FEATURE [TechDraw::DrawViewDimension] Dimension035
  AngleOverride = false
  Arbitrary = false
  ArbitraryTolerances = false
  EqualTolerance = true
  ExtensionAngle = 0
  FormatSpec = %.2w
  FormatSpecOverTolerance = %+.2w
  FormatSpecUnderTolerance = %+.2w
  Inverted = false
  LineAngle = 0
  LockPosition = false
  MeasureType = 1
  OverTolerance = 0
  References2D = -> [View003]
  Rotation = 0
  ScaleType = 2
  TheoreticalExact = false
  Type = 1
  UnderTolerance = 0
  X = -0.71045
  Y = 18.2228
FEATURE [TechDraw::DrawViewDimension] Dimension036
  AngleOverride = false
  Arbitrary = false
  ArbitraryTolerances = false
  EqualTolerance = true
  ExtensionAngle = 0
  FormatSpec = %.2w
  FormatSpecOverTolerance = %+.2w
  FormatSpecUnderTolerance = %+.2w
  Inverted = false
  LineAngle = 0
  LockPosition = false
  MeasureType = 1
  OverTolerance = 0
  References2D = -> [View003]
  Rotation = 0
  ScaleType = 2
  TheoreticalExact = false
  Type = 2
  UnderTolerance = 0
  X = 49.9751
  Y = 1.08872
FEATURE [TechDraw::DrawViewDimension] Dimension037
  AngleOverride = false
  Arbitrary = false
  ArbitraryTolerances = false
  EqualTolerance = true
  ExtensionAngle = 0
  FormatSpec = R%.2w
  FormatSpecOverTolerance = %+.2w
  FormatSpecUnderTolerance = %+.2w
  Inverted = false
  LineAngle = 0
  LockPosition = false
  MeasureType = 1
  OverTolerance = 0
  References2D = -> [View003]
  Rotation = 0
  ScaleType = 2
  TheoreticalExact = false
  Type = 4
  UnderTolerance = 0
  X = -44.9665
  Y = 11.9632
FEATURE [TechDraw::DrawViewDimension] Dimension038
  AngleOverride = false
  Arbitrary = false
  ArbitraryTolerances = false
  EqualTolerance = true
  ExtensionAngle = 0
  FormatSpec = ⌀%.3w
  FormatSpecOverTolerance = %+.2w
  FormatSpecUnderTolerance = %+.2w
  Inverted = false
  LineAngle = 0
  LockPosition = false
  MeasureType = 1
  OverTolerance = 0
  References2D = -> [View003]
  Rotation = 0
  ScaleType = 2
  TheoreticalExact = false
  Type = 5
  UnderTolerance = 0
  X = -48.5576
  Y = -11.1227
FEATURE [TechDraw::DrawViewDimension] Dimension039
  AngleOverride = false
  Arbitrary = false
  ArbitraryTolerances = false
  EqualTolerance = true
  ExtensionAngle = 0
  FormatSpec = %.2w
  FormatSpecOverTolerance = %+.2w
  FormatSpecUnderTolerance = %+.2w
  Inverted = false
  LineAngle = 0
  LockPosition = false
  MeasureType = 1
  OverTolerance = 0
  References2D = -> [View002]
  Rotation = 0
  ScaleType = 2
  TheoreticalExact = false
  Type = 1
  UnderTolerance = 0
  X = 3.68994
  Y = 19.3482
FEATURE [TechDraw::DrawViewAnnotation] Annotation
  Font = osifont
  LineSpace = 80
  LockPosition = false
  MaxWidth = -1
  Rotation = 0
  ScaleType = 2
  Text = All holes measuring 0.089" | to be tappped to fit | #4-40 threadesd screws
  TextSize = 5.08
  TextStyle = 0
  X = 47.6235
  Y = 17.1919
FEATURE [TechDraw::DrawViewDimension] Dimension043
  AngleOverride = false
  Arbitrary = false
  ArbitraryTolerances = false
  EqualTolerance = true
  ExtensionAngle = 0
  FormatSpec = %.2w
  FormatSpecOverTolerance = %+.2w
  FormatSpecUnderTolerance = %+.2w
  Inverted = false
  LineAngle = 0
  LockPosition = false
  MeasureType = 1
  OverTolerance = 0
  References2D = -> [View003]
  Rotation = 0
  ScaleType = 2
  TheoreticalExact = false
  Type = 1
  UnderTolerance = 0
  X = 1.19959
  Y = -10.9166
FEATURE [TechDraw::DrawViewDimension] Dimension044
  AngleOverride = false
  Arbitrary = false
  ArbitraryTolerances = false
  EqualTolerance = true
  ExtensionAngle = 0
  FormatSpec = R%.2w
  FormatSpecOverTolerance = %+.2w
  FormatSpecUnderTolerance = %+.2w
  Inverted = false
  LineAngle = 0
  LockPosition = false
  MeasureType = 1
  OverTolerance = 0
  References2D = -> [View001]
  Rotation = 0
  ScaleType = 2
  TheoreticalExact = false
  Type = 4
  UnderTolerance = 0
  X = -19.5101
  Y = 16.7287
FEATURE [TechDraw::DrawViewDimension] Dimension045
  AngleOverride = false
  Arbitrary = false
  ArbitraryTolerances = false
  EqualTolerance = true
  ExtensionAngle = 0
  FormatSpec = %.2w
  FormatSpecOverTolerance = %+.2w
  FormatSpecUnderTolerance = %+.2w
  Inverted = false
  LineAngle = 0
  LockPosition = false
  MeasureType = 1
  OverTolerance = 0
  References2D = -> [View001]
  Rotation = 0
  ScaleType = 2
  TheoreticalExact = false
  Type = 1
  UnderTolerance = 0
  X = -25.8878
  Y = -3.29362
FEATURE [Sketcher::SketchObject] Sketch013
  ExternalGeometry = -> [DatumLine,Pocket002,DatumLine001]
  FullyConstrained = true
  MapMode = 5
  Placement = pos=(0,0,71.9309) rot=(0,0,1;0rad)
  Support = -> [Pocket002]
  sketch-geometry (4):
    g0: Circle CenterX=58.8476 CenterY=-61.0824 CenterZ=0 NormalX=0 NormalY=0 NormalZ=1 AngleXU=0 Radius=4.0005
    g1: Circle CenterX=58.8476 CenterY=-92.5142 CenterZ=0 NormalX=0 NormalY=0 NormalZ=1 AngleXU=0 Radius=4.0005
    g2: LineSegment StartX=77.2643 StartY=-58.015 StartZ=0 EndX=77.2643 EndY=-96.0134 EndZ=0
    g3: LineSegment StartX=40.4309 StartY=-92.5142 StartZ=0 EndX=77.2643 EndY=-92.5142 EndZ=0
  constraints (10):
    c: Coincident(g2,g-4)
    c: Coincident(g2,g-7)
    c: Coincident(g3,g-6)
    c: PointOnObject(g3,g2)
    c: Horizontal(g3)
    c: Vertical(g1,g0)
    c: Horizontal(g0,g-5)
    c: Equal(g1,g0)
    c: Diameter(g0) = 8.001
    c: Symmetric(g3,g3,g1)
FEATURE [PartDesign::Pocket] Pocket003  label="LED_Holes"
  BaseFeature = -> Pocket002
  Direction = (0,0,-1)
  Length = 5
  Length2 = 5
  Profile = -> Sketch013
  ReferenceAxis = -> Sketch013 [N_Axis]
  Type = 1
FEATURE [Sketcher::SketchObject] Sketch014
  FullyConstrained = false
  MapMode = 5
  Placement = pos=(0,0,71.9309) rot=(0,0,1;0rad)
  Support = -> [Pocket003]
  expr: Constraints[0] = Sketch013.Constraints[8]
  sketch-geometry (1):
    g0: Circle CenterX=25.9963 CenterY=-159.179 CenterZ=0 NormalX=0 NormalY=0 NormalZ=1 AngleXU=0 Radius=4.0005
  constraints (1):
    c: Diameter(g0) = 8.001
FEATURE [PartDesign::Body] Body
  BaseFeature = -> BaseFeature001
  Group = -> [BaseFeature,Sketch002,Sketch004,DatumLine,DatumLine001,ReferencePart__Feature041002002,ReferencePart__Feature041002002001,Sketch008,Sketch009,Sketch011,Pocket,Pocket001,Pocket002,Sketch012,Sketch,Sketch013,Pocket003,Sketch014]
  Origin = -> Origin
  Placement = pos=(44.82,89.43,-3.8) rot=(0,0,1;0rad)
  Tip = -> Pocket003
FEATURE [TechDraw::DrawViewPart] View004
  CoarseView = false
  Direction = (0,0,1)
  Focus = 100
  HardHidden = false
  IsoCount = 0
  IsoHidden = false
  IsoVisible = false
  LockPosition = false
  Perspective = false
  Rotation = 0
  ScaleType = 0
  SeamHidden = false
  SeamVisible = true
  SmoothHidden = false
  SmoothVisible = true
  Source = -> [Sketch014]
  X = 139.415
  XDirection = (1,0,0)
  Y = 162.113
FEATURE [TechDraw::DrawViewDimension] Dimension046
  AngleOverride = false
  Arbitrary = false
  ArbitraryTolerances = false
  EqualTolerance = true
  ExtensionAngle = 0
  FormatSpec = ⌀%.3w
  FormatSpecOverTolerance = %+.2w
  FormatSpecUnderTolerance = %+.2w
  Inverted = false
  LineAngle = 0
  LockPosition = false
  MeasureType = 1
  OverTolerance = 0
  References2D = -> [View004]
  Rotation = 0
  ScaleType = 0
  TheoreticalExact = false
  Type = 5
  UnderTolerance = 0
  X = -5.18068
  Y = 17.5633
FEATURE [TechDraw::DrawViewPart] View  label="Front_Panel"
  CoarseView = false
  Direction = (0,0,1)
  Focus = 100
  HardHidden = false
  IsoCount = 0
  IsoHidden = false
  IsoVisible = false
  LockPosition = false
  Perspective = false
  Rotation = 0
  Scale = 0.6
  ScaleType = 2
  SeamHidden = false
  SeamVisible = true
  SmoothHidden = false
  SmoothVisible = true
  Source = -> [Body]
  X = 150.048
  XDirection = (1,0,0)
  Y = 97.4782
FEATURE [TechDraw::DrawViewDimension] Dimension050
  AngleOverride = false
  Arbitrary = false
  ArbitraryTolerances = false
  EqualTolerance = true
  ExtensionAngle = 0
  FormatSpec = %.2w
  FormatSpecOverTolerance = %+.2w
  FormatSpecUnderTolerance = %+.2w
  Inverted = false
  LineAngle = 0
  LockPosition = false
  MeasureType = 1
  OverTolerance = 0
  References2D = -> [View]
  Rotation = 0
  ScaleType = 0
  TheoreticalExact = false
  Type = 2
  UnderTolerance = 0
  X = 113.722
  Y = 0.771992
FEATURE [TechDraw::DrawViewDimension] Dimension051
  AngleOverride = false
  Arbitrary = false
  ArbitraryTolerances = false
  EqualTolerance = true
  ExtensionAngle = 0
  FormatSpec = %.2w
  FormatSpecOverTolerance = %+.2w
  FormatSpecUnderTolerance = %+.2w
  Inverted = false
  LineAngle = 0
  LockPosition = false
  MeasureType = 1
  OverTolerance = 0
  References2D = -> [View]
  Rotation = 0
  ScaleType = 0
  TheoreticalExact = false
  Type = 2
  UnderTolerance = 0
  X = 70.259
  Y = -24.1678
FEATURE [TechDraw::DrawViewDimension] Dimension052
  AngleOverride = false
  Arbitrary = false
  ArbitraryTolerances = false
  EqualTolerance = true
  ExtensionAngle = 0
  FormatSpec = %.2w
  FormatSpecOverTolerance = %+.2w
  FormatSpecUnderTolerance = %+.2w
  Inverted = false
  LineAngle = 0
  LockPosition = false
  MeasureType = 1
  OverTolerance = 0
  References2D = -> [View]
  Rotation = 0
  ScaleType = 0
  TheoreticalExact = false
  Type = 1
  UnderTolerance = 0
  X = 97.8705
  Y = -26.9363
FEATURE [TechDraw::DrawViewDimension] Dimension053
  AngleOverride = false
  Arbitrary = false
  ArbitraryTolerances = false
  EqualTolerance = true
  ExtensionAngle = 0
  FormatSpec = %.2w
  FormatSpecOverTolerance = %+.2w
  FormatSpecUnderTolerance = %+.2w
  Inverted = false
  LineAngle = 0
  LockPosition = false
  MeasureType = 1
  OverTolerance = 0
  References2D = -> [View]
  Rotation = 0
  ScaleType = 0
  TheoreticalExact = false
  Type = 1
  UnderTolerance = 0
  X = 37.1195
  Y = -18.566
FEATURE [TechDraw::DrawViewDimension] Dimension054
  AngleOverride = false
  Arbitrary = false
  ArbitraryTolerances = false
  EqualTolerance = true
  ExtensionAngle = 0
  FormatSpec = %.2w
  FormatSpecOverTolerance = %+.2w
  FormatSpecUnderTolerance = %+.2w
  Inverted = false
  LineAngle = 0
  LockPosition = false
  MeasureType = 1
  OverTolerance = 0
  References2D = -> [View]
  Rotation = 0
  ScaleType = 0
  TheoreticalExact = false
  Type = 2
  UnderTolerance = 0
  X = 11.5573
  Y = 27.7412
FEATURE [TechDraw::DrawViewDimension] Dimension055
  AngleOverride = false
  Arbitrary = false
  ArbitraryTolerances = false
  EqualTolerance = true
  ExtensionAngle = 0
  FormatSpec = %.2w
  FormatSpecOverTolerance = %+.2w
  FormatSpecUnderTolerance = %+.2w
  Inverted = false
  LineAngle = 0
  LockPosition = false
  MeasureType = 1
  OverTolerance = 0
  References2D = -> [View]
  Rotation = 0
  ScaleType = 0
  TheoreticalExact = false
  Type = 2
  UnderTolerance = 0
  X = -4.11543
  Y = 2.83094
FEATURE [TechDraw::DrawViewDimension] Dimension056
  AngleOverride = false
  Arbitrary = false
  ArbitraryTolerances = false
  EqualTolerance = true
  ExtensionAngle = 0
  FormatSpec = %.2w
  FormatSpecOverTolerance = %+.2w
  FormatSpecUnderTolerance = %+.2w
  Inverted = false
  LineAngle = 0
  LockPosition = false
  MeasureType = 1
  OverTolerance = 0
  References2D = -> [View]
  Rotation = 0
  ScaleType = 0
  TheoreticalExact = false
  Type = 2
  UnderTolerance = 0
  X = -4.59962
  Y = -26.1291
FEATURE [TechDraw::DrawViewDimension] Dimension057
  AngleOverride = false
  Arbitrary = false
  ArbitraryTolerances = false
  EqualTolerance = true
  ExtensionAngle = 0
  FormatSpec = %.2w
  FormatSpecOverTolerance = %+.2w
  FormatSpecUnderTolerance = %+.2w
  Inverted = false
  LineAngle = 0
  LockPosition = false
  MeasureType = 1
  OverTolerance = 0
  References2D = -> [View]
  Rotation = 0
  ScaleType = 0
  TheoreticalExact = false
  Type = 1
  UnderTolerance = 0
  X = 44.0425
  Y = -40.8888
FEATURE [TechDraw::DrawViewDimension] Dimension058
  AngleOverride = false
  Arbitrary = false
  ArbitraryTolerances = false
  EqualTolerance = true
  ExtensionAngle = 0
  FormatSpec = %.2w
  FormatSpecOverTolerance = %+.2w
  FormatSpecUnderTolerance = %+.2w
  Inverted = false
  LineAngle = 0
  LockPosition = false
  MeasureType = 1
  OverTolerance = 0
  References2D = -> [View]
  Rotation = 0
  ScaleType = 0
  TheoreticalExact = false
  Type = 1
  UnderTolerance = 0
  X = 61.713
  Y = 30.1426
FEATURE [TechDraw::DrawViewDimension] Dimension059
  AngleOverride = false
  Arbitrary = false
  ArbitraryTolerances = false
  EqualTolerance = true
  ExtensionAngle = 0
  FormatSpec = %.2w
  FormatSpecOverTolerance = %+.2w
  FormatSpecUnderTolerance = %+.2w
  Inverted = false
  LineAngle = 0
  LockPosition = false
  MeasureType = 1
  OverTolerance = 0
  References2D = -> [View]
  Rotation = 0
  ScaleType = 0
  TheoreticalExact = false
  Type = 2
  UnderTolerance = 0
  X = 64.8097
  Y = 2.3308
FEATURE [TechDraw::DrawViewDimension] Dimension061
  AngleOverride = false
  Arbitrary = false
  ArbitraryTolerances = false
  EqualTolerance = true
  ExtensionAngle = 0
  FormatSpec = %.2w
  FormatSpecOverTolerance = %+.2w
  FormatSpecUnderTolerance = %+.2w
  Inverted = false
  LineAngle = 0
  LockPosition = false
  MeasureType = 1
  OverTolerance = 0
  References2D = -> [View]
  Rotation = 0
  ScaleType = 0
  TheoreticalExact = false
  Type = 2
  UnderTolerance = 0
  X = -118.238
  Y = 2.32784
FEATURE [TechDraw::DrawViewDimension] Dimension062
  AngleOverride = false
  Arbitrary = false
  ArbitraryTolerances = false
  EqualTolerance = true
  ExtensionAngle = 0
  FormatSpec = %.2w
  FormatSpecOverTolerance = %+.2w
  FormatSpecUnderTolerance = %+.2w
  Inverted = false
  LineAngle = 0
  LockPosition = false
  MeasureType = 1
  OverTolerance = 0
  References2D = -> [View]
  Rotation = 0
  ScaleType = 0
  TheoreticalExact = false
  Type = 1
  UnderTolerance = 0
  X = -76.7917
  Y = -25.9196
FEATURE [TechDraw::DrawViewDimension] Dimension063
  AngleOverride = false
  Arbitrary = false
  ArbitraryTolerances = false
  EqualTolerance = true
  ExtensionAngle = 0
  FormatSpec = %.2w
  FormatSpecOverTolerance = %+.2w
  FormatSpecUnderTolerance = %+.2w
  Inverted = false
  LineAngle = 0
  LockPosition = false
  MeasureType = 1
  OverTolerance = 0
  References2D = -> [View]
  Rotation = 0
  ScaleType = 0
  TheoreticalExact = false
  Type = 2
  UnderTolerance = 0
  X = -119.01
  Y = -28.6755
FEATURE [TechDraw::DrawPage] Page  label="Front_Panel_Drawing"
  KeepUpdated = true
  NextBalloonIndex = 1
  ProjectionType = 0
  Template = -> Template
  Views = -> [View,View001,View002,View003,Dimension,Dimension007,Dimension010,Dimension011,Dimension018,Dimension019,Dimension022,Dimension023,Dimension026,Dimension027,Dimension034,Dimension035,Dimension036,Dimension037,Dimension038,Dimension039,Annotation,Dimension043,Dimension044,Dimension045,View004,Dimension046,Dimension050,Dimension051,Dimension052,Dimension053,Dimension054,Dimension055,Dimension056,+6 more]
